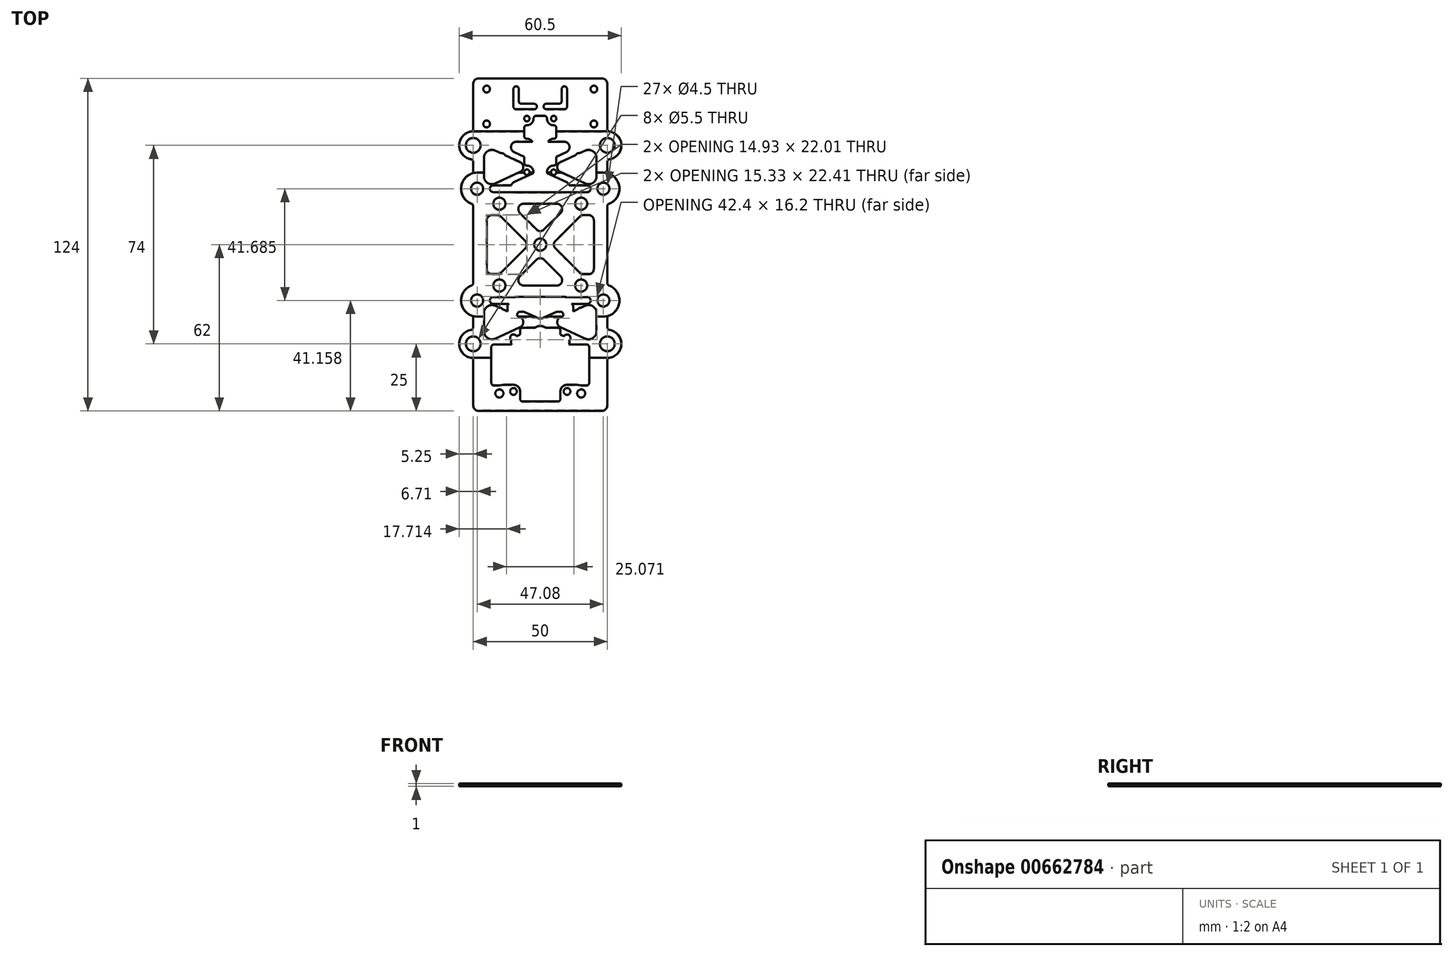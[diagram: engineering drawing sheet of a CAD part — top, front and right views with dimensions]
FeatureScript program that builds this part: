
annotation { "Feature Type Name" : "Feature", "Feature Type Description" : "" }
export const myFeature = defineFeature(function(context is Context, id is Id, definition is map)
    precondition{}
    {
        {
            var Q0;
            Q0=qCreatedBy(makeId("Top.planeOp"),FACE);
            var sketch = newSketch(context, id + "F0", { "sketchPlane" : qUnion([Q0])});
            skLineSegment(sketch, "E0.bottom", {"start": v(15.25, 15.25) * mm, "end": v(-15.25, 15.25) * mm, "construction": true});
            skLineSegment(sketch, "E0.top", {"start": v(15.25, -15.25) * mm, "end": v(-15.25, -15.25) * mm, "construction": true});
            skLineSegment(sketch, "E0.left", {"start": v(15.25, 15.25) * mm, "end": v(15.25, -15.25) * mm, "construction": true});
            skLineSegment(sketch, "E0.right", {"start": v(-15.25, 15.25) * mm, "end": v(-15.25, -15.25) * mm, "construction": true});
            skPoint(sketch, "E0.middle", {"position": v(0, 0) * mm});
            skLineSegment(sketch, "E1", {"start": v(15.25, 15.25) * mm, "end": v(23.54, 20.84) * mm});
            skLineSegment(sketch, "E2", {"start": v(23.54, 20.84) * mm, "end": v(92.7, 67.5) * mm});
            skCircle(sketch, "E3", {"center": v(92.7, 67.5) * mm, "radius": 63.5 * mm, "construction": true});
            skLineSegment(sketch, "E4", {"start": v(0, 0) * mm, "end": v(92.7, 0) * mm, "construction": true});
            skLineSegment(sketch, "E5.bottom", {"start": v(-25, 37) * mm, "end": v(25, 37) * mm, "construction": true});
            skLineSegment(sketch, "E5.top", {"start": v(-25, -37) * mm, "end": v(25, -37) * mm, "construction": true});
            skLineSegment(sketch, "E5.left", {"start": v(-25, 37) * mm, "end": v(-25, -37) * mm, "construction": true});
            skLineSegment(sketch, "E5.right", {"start": v(25, 37) * mm, "end": v(25, -37) * mm, "construction": true});
            skCircle(sketch, "E6", {"center": v(25, 37) * mm, "radius": 4.25 * mm, "construction": true});
            skCircle(sketch, "E7", {"center": v(15.25, 15.25) * mm, "radius": 1.5 * mm, "construction": true});
            skCircle(sketch, "E8", {"center": v(23.54, 20.84) * mm, "radius": 1.5 * mm, "construction": true});
            skCircle(sketch, "E9", {"center": v(92.7, 67.5) * mm, "radius": 50.8 * mm, "construction": true});
            skLineSegment(sketch, "E10.bottom", {"start": v(11.34, 21.05) * mm, "end": v(88.79, 73.3) * mm, "construction": true});
            skLineSegment(sketch, "E10.top", {"start": v(19.16, 9.45) * mm, "end": v(96.62, 61.7) * mm, "construction": true});
            skLineSegment(sketch, "E10.left", {"start": v(11.34, 21.05) * mm, "end": v(19.16, 9.45) * mm, "construction": true});
            skLineSegment(sketch, "E10.right", {"start": v(88.79, 73.3) * mm, "end": v(96.62, 61.7) * mm, "construction": true});
            skCircle(sketch, "E11", {"center": v(-25, 37) * mm, "radius": 4.25 * mm, "construction": true});
            skCircle(sketch, "E12", {"center": v(-25, -37) * mm, "radius": 4.25 * mm, "construction": true});
            skCircle(sketch, "E13", {"center": v(25, -37) * mm, "radius": 4.25 * mm, "construction": true});
            skCircle(sketch, "E14", {"center": v(-15.25, 15.25) * mm, "radius": 1.5 * mm, "construction": true});
            skCircle(sketch, "E15", {"center": v(-15.25, -15.25) * mm, "radius": 1.5 * mm, "construction": true});
            skCircle(sketch, "E16", {"center": v(15.25, -15.25) * mm, "radius": 1.5 * mm, "construction": true});
            skCircle(sketch, "E17.MirrorC", {"center": v(-23.54, 20.84) * mm, "radius": 1.5 * mm, "construction": true});
            skCircle(sketch, "E18.MirrorC", {"center": v(-23.54, -20.84) * mm, "radius": 1.5 * mm, "construction": true});
            skCircle(sketch, "E19.MirrorC", {"center": v(23.54, -20.84) * mm, "radius": 1.5 * mm, "construction": true});
            skSolve(sketch);
        }
        {
            var Q0;
            Q0=qCreatedBy(makeId("Top.planeOp"),FACE);
            var sketch = newSketch(context, id + "F1", { "sketchPlane" : qUnion([Q0])});
            skPoint(sketch, "E20.0", {"position": v(-25, 37) * mm});
            skPoint(sketch, "E21.0", {"position": v(25, 37) * mm});
            skPoint(sketch, "E22.0", {"position": v(25, -37) * mm});
            skPoint(sketch, "E23.0", {"position": v(-25, -37) * mm});
            skCircle(sketch, "E24.0", {"center": v(-23.54, -20.84) * mm, "radius": 1.55 * mm});
            skCircle(sketch, "E25.0", {"center": v(-15.25, -15.25) * mm, "radius": 1.55 * mm});
            skCircle(sketch, "E26.0", {"center": v(15.25, -15.25) * mm, "radius": 1.55 * mm});
            skCircle(sketch, "E27.0", {"center": v(23.54, -20.84) * mm, "radius": 1.55 * mm});
            skCircle(sketch, "E28.0", {"center": v(15.25, 15.25) * mm, "radius": 1.55 * mm});
            skCircle(sketch, "E29.0", {"center": v(-15.25, 15.25) * mm, "radius": 1.55 * mm});
            skCircle(sketch, "E30.0", {"center": v(-23.54, 20.84) * mm, "radius": 1.55 * mm});
            skCircle(sketch, "E31.0", {"center": v(23.54, 20.84) * mm, "radius": 1.55 * mm});
            skCircle(sketch, "E32", {"center": v(25, 37) * mm, "radius": 2.75 * mm});
            skCircle(sketch, "E33", {"center": v(-25, 37) * mm, "radius": 2.75 * mm});
            skCircle(sketch, "E34", {"center": v(-25, -37) * mm, "radius": 2.75 * mm});
            skCircle(sketch, "E35", {"center": v(25, -37) * mm, "radius": 2.75 * mm});
            skSolve(sketch);
        }
        {
            var Q0;
            Q0=qCreatedBy(makeId("Top.planeOp"),FACE);
            var sketch = newSketch(context, id + "F2", { "sketchPlane" : qUnion([Q0])});
            skCircle(sketch, "E36.0", {"center": v(-25, -37) * mm, "radius": 2.75 * mm});
            skCircle(sketch, "E37.0", {"center": v(-23.54, -20.84) * mm, "radius": 1.55 * mm});
            skCircle(sketch, "E38.0", {"center": v(-15.25, -15.25) * mm, "radius": 1.55 * mm});
            skCircle(sketch, "E39.0", {"center": v(15.25, -15.25) * mm, "radius": 1.55 * mm});
            skCircle(sketch, "E40.0", {"center": v(23.54, -20.84) * mm, "radius": 1.55 * mm});
            skCircle(sketch, "E41.0", {"center": v(-25, 37) * mm, "radius": 2.75 * mm});
            skCircle(sketch, "E42.0", {"center": v(-23.54, 20.84) * mm, "radius": 1.55 * mm});
            skCircle(sketch, "E43.0", {"center": v(-15.25, 15.25) * mm, "radius": 1.55 * mm});
            skCircle(sketch, "E44.0", {"center": v(15.25, 15.25) * mm, "radius": 1.55 * mm});
            skCircle(sketch, "E45.0", {"center": v(23.54, 20.84) * mm, "radius": 1.55 * mm});
            skCircle(sketch, "E46.0", {"center": v(25, 37) * mm, "radius": 2.75 * mm});
            skLineSegment(sketch, "E47.bottom", {"start": v(25, 62) * mm, "end": v(-25, 62) * mm});
            skLineSegment(sketch, "E47.top", {"start": v(25, -62) * mm, "end": v(-25, -62) * mm});
            skLineSegment(sketch, "E47.left", {"start": v(25, 62) * mm, "end": v(25, 42.25) * mm});
            skLineSegment(sketch, "E47.right", {"start": v(-25, 62) * mm, "end": v(-25, 42.25) * mm});
            skPoint(sketch, "E47.middle", {"position": v(0, 0) * mm});
            skArc(sketch, "E48", {"start": v(-25, 42.25) * mm, "mid": v(-30.25, 37) * mm, "end": v(-25, 31.75) * mm});
            skArc(sketch, "E49", {"start": v(-25, 26.66) * mm, "mid": v(-29.54, 20.84) * mm, "end": v(-25, 15.02) * mm});
            skArc(sketch, "E50", {"start": v(-25, -15.02) * mm, "mid": v(-29.54, -20.84) * mm, "end": v(-25, -26.66) * mm});
            skArc(sketch, "E51.MirrorCS", {"start": v(25, 42.25) * mm, "mid": v(30.25, 37) * mm, "end": v(25, 31.75) * mm});
            skArc(sketch, "E52.MirrorCS", {"start": v(25, 26.66) * mm, "mid": v(29.54, 20.84) * mm, "end": v(25, 15.02) * mm});
            skArc(sketch, "E53.MirrorCS", {"start": v(25, -15.02) * mm, "mid": v(29.54, -20.84) * mm, "end": v(25, -26.66) * mm});
            skArc(sketch, "E54", {"start": v(-25, -31.75) * mm, "mid": v(-30.25, -37) * mm, "end": v(-25, -42.25) * mm});
            skArc(sketch, "E55.MirrorCS", {"start": v(25, -31.75) * mm, "mid": v(30.25, -37) * mm, "end": v(25, -42.25) * mm});
            skLineSegment(sketch, "E56", {"start": v(-25, 42.25) * mm, "end": v(-25, 39.75) * mm, "construction": true});
            skLineSegment(sketch, "E57", {"start": v(-25, 31.75) * mm, "end": v(-25, 26.66) * mm});
            skLineSegment(sketch, "E58", {"start": v(-25, 34.25) * mm, "end": v(-25, 31.75) * mm, "construction": true});
            skLineSegment(sketch, "E59", {"start": v(-25, 39.75) * mm, "end": v(-25, 34.25) * mm, "construction": true});
            skLineSegment(sketch, "E60", {"start": v(25, 39.75) * mm, "end": v(25, 34.25) * mm, "construction": true});
            skLineSegment(sketch, "E61", {"start": v(25, 42.25) * mm, "end": v(25, 39.75) * mm, "construction": true});
            skLineSegment(sketch, "E62", {"start": v(25, 34.25) * mm, "end": v(25, 31.75) * mm, "construction": true});
            skLineSegment(sketch, "E63", {"start": v(25, 31.75) * mm, "end": v(25, 26.66) * mm});
            skLineSegment(sketch, "E64", {"start": v(-25, 26.66) * mm, "end": v(-25, 15.02) * mm, "construction": true});
            skLineSegment(sketch, "E65", {"start": v(-25, 15.02) * mm, "end": v(-25, -15.02) * mm});
            skLineSegment(sketch, "E66", {"start": v(25, 26.66) * mm, "end": v(25, 15.02) * mm, "construction": true});
            skLineSegment(sketch, "E67", {"start": v(25, 15.02) * mm, "end": v(25, -15.02) * mm});
            skLineSegment(sketch, "E68", {"start": v(-25, -31.75) * mm, "end": v(-25, -34.25) * mm, "construction": true});
            skLineSegment(sketch, "E69", {"start": v(-25, -42.25) * mm, "end": v(-25, -62) * mm});
            skLineSegment(sketch, "E70", {"start": v(-25, -39.75) * mm, "end": v(-25, -42.25) * mm, "construction": true});
            skLineSegment(sketch, "E71", {"start": v(-25, -34.25) * mm, "end": v(-25, -39.75) * mm, "construction": true});
            skLineSegment(sketch, "E72", {"start": v(-25, -26.66) * mm, "end": v(-25, -31.75) * mm});
            skLineSegment(sketch, "E73", {"start": v(-25, -15.02) * mm, "end": v(-25, -26.66) * mm, "construction": true});
            skLineSegment(sketch, "E74", {"start": v(25, -15.02) * mm, "end": v(25, -26.66) * mm});
            skLineSegment(sketch, "E75", {"start": v(25, -26.66) * mm, "end": v(25, -31.75) * mm});
            skLineSegment(sketch, "E76", {"start": v(25, -31.75) * mm, "end": v(25, -42.25) * mm, "construction": true});
            skLineSegment(sketch, "E77", {"start": v(25, -42.25) * mm, "end": v(25, -42.25) * mm});
            skArc(sketch, "E78", {"start": v(25, -34.25) * mm, "mid": v(22.25, -37) * mm, "end": v(25, -39.75) * mm});
            skArc(sketch, "E79", {"start": v(25, -39.75) * mm, "mid": v(27.75, -37) * mm, "end": v(25, -34.25) * mm});
            skLineSegment(sketch, "E80", {"start": v(25, -42.25) * mm, "end": v(25, -62) * mm});
            skSolve(sketch);
        }
        {
            var Q0;
            Q0 = qSketchRegion(id + "F2", true);
            extrude(context, id + "F3", {"entities" : qUnion([Q0]), "depth" : 1 * mm, "offsetDistance" : 25 * mm});
        }
        {
            var Q0;
            Q0=qCreatedBy(makeId("Top.planeOp"),FACE);
            var sketch = newSketch(context, id + "F4", { "sketchPlane" : qUnion([Q0])});
            skCircle(sketch, "E81.0", {"center": v(-23.54, 20.84) * mm, "radius": 1.55 * mm});
            skCircle(sketch, "E82.0", {"center": v(-15.25, 15.25) * mm, "radius": 1.55 * mm});
            skCircle(sketch, "E83.0", {"center": v(15.25, 15.25) * mm, "radius": 1.55 * mm});
            skCircle(sketch, "E84.0", {"center": v(23.54, 20.84) * mm, "radius": 1.55 * mm});
            skCircle(sketch, "E85.0", {"center": v(-15.25, -15.25) * mm, "radius": 1.55 * mm});
            skCircle(sketch, "E86.0", {"center": v(-23.54, -20.84) * mm, "radius": 1.55 * mm});
            skCircle(sketch, "E87.0", {"center": v(15.25, -15.25) * mm, "radius": 1.55 * mm});
            skCircle(sketch, "E88.0", {"center": v(23.54, -20.84) * mm, "radius": 1.55 * mm});
            skArc(sketch, "E89.0", {"start": v(-25, 26.66) * mm, "mid": v(-29.54, 20.84) * mm, "end": v(-25, 15.02) * mm});
            skLineSegment(sketch, "E90.0", {"start": v(-25, 15.02) * mm, "end": v(-25, -15.02) * mm});
            skArc(sketch, "E91.0", {"start": v(-25, -15.02) * mm, "mid": v(-29.54, -20.84) * mm, "end": v(-25, -26.66) * mm});
            skLineSegment(sketch, "E92.0", {"start": v(25, 15.02) * mm, "end": v(25, -15.02) * mm});
            skArc(sketch, "E93.0", {"start": v(25, 26.66) * mm, "mid": v(29.54, 20.84) * mm, "end": v(25, 15.02) * mm});
            skArc(sketch, "E94.0", {"start": v(25, -15.02) * mm, "mid": v(29.54, -20.84) * mm, "end": v(25, -26.66) * mm});
            skArc(sketch, "E95", {"start": v(-25, 26.66) * mm, "mid": v(-24.28, 26.8) * mm, "end": v(-23.54, 26.84) * mm});
            skArc(sketch, "E96", {"start": v(-25, -26.66) * mm, "mid": v(-24.28, -26.8) * mm, "end": v(-23.54, -26.84) * mm});
            skArc(sketch, "E97", {"start": v(25, 26.66) * mm, "mid": v(24.28, 26.8) * mm, "end": v(23.54, 26.84) * mm});
            skArc(sketch, "E98", {"start": v(25, -26.66) * mm, "mid": v(24.28, -26.8) * mm, "end": v(23.54, -26.84) * mm});
            skLineSegment(sketch, "E99", {"start": v(-23.54, 26.84) * mm, "end": v(23.54, 26.84) * mm});
            skLineSegment(sketch, "E100", {"start": v(-23.54, -26.84) * mm, "end": v(23.54, -26.84) * mm});
            skSolve(sketch);
        }
        {
            var Q0;
            Q0=qCreatedBy(makeId("Top.planeOp"),FACE);
            var sketch = newSketch(context, id + "F5", { "sketchPlane" : qUnion([Q0])});
            skArc(sketch, "E101.0.0", {"start": v(25, -26.66) * mm, "mid": v(29.54, -20.84) * mm, "end": v(25, -15.02) * mm});
            skLineSegment(sketch, "E101.0.1", {"start": v(25, -15.02) * mm, "end": v(25, 15.02) * mm});
            skArc(sketch, "E101.0.2", {"start": v(25, 15.02) * mm, "mid": v(29.54, 20.84) * mm, "end": v(25, 26.66) * mm});
            skLineSegment(sketch, "E101.0.3", {"start": v(25, 26.66) * mm, "end": v(25, 31.75) * mm});
            skArc(sketch, "E101.0.4", {"start": v(25, 31.75) * mm, "mid": v(30.25, 37) * mm, "end": v(25, 42.25) * mm});
            skLineSegment(sketch, "E101.0.5", {"start": v(25, 42.25) * mm, "end": v(25, 62) * mm});
            skLineSegment(sketch, "E101.0.6", {"start": v(25, 62) * mm, "end": v(-25, 62) * mm, "construction": true});
            skLineSegment(sketch, "E101.0.7", {"start": v(-25, 62) * mm, "end": v(-25, 42.25) * mm});
            skArc(sketch, "E101.0.8", {"start": v(-25, 42.25) * mm, "mid": v(-30.25, 37) * mm, "end": v(-25, 31.75) * mm});
            skLineSegment(sketch, "E101.0.9", {"start": v(-25, 31.75) * mm, "end": v(-25, 26.66) * mm});
            skArc(sketch, "E101.0.10", {"start": v(-25, 26.66) * mm, "mid": v(-29.54, 20.84) * mm, "end": v(-25, 15.02) * mm});
            skLineSegment(sketch, "E101.0.11", {"start": v(-25, 15.02) * mm, "end": v(-25, -15.02) * mm});
            skArc(sketch, "E101.0.12", {"start": v(-25, -15.02) * mm, "mid": v(-29.54, -20.84) * mm, "end": v(-25, -26.66) * mm});
            skLineSegment(sketch, "E101.0.13", {"start": v(-25, -26.66) * mm, "end": v(-25, -31.75) * mm});
            skArc(sketch, "E101.0.14", {"start": v(-25, -31.75) * mm, "mid": v(-30.25, -37) * mm, "end": v(-25, -42.25) * mm});
            skLineSegment(sketch, "E101.0.15", {"start": v(-25, -42.25) * mm, "end": v(-25, -62) * mm});
            skLineSegment(sketch, "E101.0.16", {"start": v(-25, -62) * mm, "end": v(25, -62) * mm, "construction": true});
            skLineSegment(sketch, "E101.0.17", {"start": v(25, -62) * mm, "end": v(25, -42.25) * mm});
            skArc(sketch, "E101.0.18", {"start": v(25, -42.25) * mm, "mid": v(30.25, -37) * mm, "end": v(25, -31.75) * mm});
            skLineSegment(sketch, "E101.0.19", {"start": v(25, -31.75) * mm, "end": v(25, -26.66) * mm});
            skLineSegment(sketch, "E102", {"start": v(-25, 42.25) * mm, "end": v(25, 42.25) * mm});
            skLineSegment(sketch, "E103", {"start": v(-25, -42.25) * mm, "end": v(25, -42.25) * mm});
            skCircle(sketch, "E104.0", {"center": v(-25, 37) * mm, "radius": 2.75 * mm});
            skCircle(sketch, "E105.0", {"center": v(-23.54, 20.84) * mm, "radius": 1.55 * mm});
            skCircle(sketch, "E106.0", {"center": v(-15.25, 15.25) * mm, "radius": 1.55 * mm});
            skCircle(sketch, "E107.0", {"center": v(15.25, 15.25) * mm, "radius": 1.55 * mm});
            skCircle(sketch, "E108.0", {"center": v(23.54, 20.84) * mm, "radius": 1.55 * mm});
            skCircle(sketch, "E109.0", {"center": v(25, 37) * mm, "radius": 2.75 * mm});
            skCircle(sketch, "E110.0", {"center": v(-23.54, -20.84) * mm, "radius": 1.55 * mm});
            skCircle(sketch, "E111.0", {"center": v(-15.25, -15.25) * mm, "radius": 1.55 * mm});
            skCircle(sketch, "E112.0", {"center": v(15.25, -15.25) * mm, "radius": 1.55 * mm});
            skCircle(sketch, "E113.0", {"center": v(23.54, -20.84) * mm, "radius": 1.55 * mm});
            skCircle(sketch, "E114.0", {"center": v(-25, -37) * mm, "radius": 2.75 * mm});
            skCircle(sketch, "E115.0", {"center": v(25, -37) * mm, "radius": 2.75 * mm});
            skSolve(sketch);
        }
        {
            var Q0;
            Q0 = qSketchRegion(id + "F4", true);
            extrude(context, id + "F6", {"entities" : qUnion([Q0]), "depth" : 1 * mm, "offsetDistance" : 25 * mm});
        }
        {
            var Q0;
            Q0 = qSketchRegion(id + "F5", true);
            extrude(context, id + "F7", {"entities" : qUnion([Q0]), "depth" : 1 * mm, "offsetDistance" : 25 * mm});
        }
        {
            var Q0;
            Q0=makeQuery(id+"F3.opExtrude","SWEPT_EDGE",EDGE,{"disambiguationData":[OSD([sQuery(id+"F2.wireOp",EDGE,"E47.top"),sQuery(id+"F2.wireOp",EDGE,"E69")])]});
            var Q1;
            Q1=makeQuery(id+"F3.opExtrude","SWEPT_EDGE",EDGE,{"disambiguationData":[OSD([sQuery(id+"F2.wireOp",EDGE,"E47.top"),sQuery(id+"F2.wireOp",EDGE,"E80")])]});
            var Q2;
            Q2=makeQuery(id+"F3.opExtrude","SWEPT_EDGE",EDGE,{"disambiguationData":[OSD([sQuery(id+"F2.wireOp",EDGE,"E47.bottom"),sQuery(id+"F2.wireOp",EDGE,"E47.right")])]});
            var Q3;
            Q3=makeQuery(id+"F3.opExtrude","SWEPT_EDGE",EDGE,{"disambiguationData":[OSD([sQuery(id+"F2.wireOp",EDGE,"E47.bottom"),sQuery(id+"F2.wireOp",EDGE,"E47.left")])]});
            fillet(context, id + "F8", {"entities" : qUnion([Q0, Q1, Q2, Q3]), "radius" : 2 * mm, "allowEdgeOverflow" : false});
        }
        {
            var Q0;
            Q0=makeQuery(id+"F3.opExtrude","SWEPT_EDGE",EDGE,{"disambiguationData":[OSD([sQuery(id+"F2.wireOp",EDGE,"E47.left"),sQuery(id+"F2.wireOp",EDGE,"E51.MirrorCS")])]});
            var Q1;
            Q1=makeQuery(id+"F3.opExtrude","SWEPT_EDGE",EDGE,{"disambiguationData":[OSD([sQuery(id+"F2.wireOp",EDGE,"E51.MirrorCS"),sQuery(id+"F2.wireOp",EDGE,"E63")])]});
            var Q2;
            Q2=makeQuery(id+"F3.opExtrude","SWEPT_EDGE",EDGE,{"disambiguationData":[OSD([sQuery(id+"F2.wireOp",EDGE,"E52.MirrorCS"),sQuery(id+"F2.wireOp",EDGE,"E63")])]});
            var Q3;
            Q3=makeQuery(id+"F3.opExtrude","SWEPT_EDGE",EDGE,{"disambiguationData":[OSD([sQuery(id+"F2.wireOp",EDGE,"E52.MirrorCS"),sQuery(id+"F2.wireOp",EDGE,"E67")])]});
            var Q4;
            Q4=makeQuery(id+"F3.opExtrude","SWEPT_EDGE",EDGE,{"disambiguationData":[OSD([sQuery(id+"F2.wireOp",EDGE,"E53.MirrorCS"),sQuery(id+"F2.wireOp",EDGE,"E67"),sQuery(id+"F2.wireOp",EDGE,"E74")])]});
            var Q5;
            Q5=makeQuery(id+"F3.opExtrude","SWEPT_EDGE",EDGE,{"disambiguationData":[OSD([sQuery(id+"F2.wireOp",EDGE,"E55.MirrorCS"),sQuery(id+"F2.wireOp",EDGE,"E75")])]});
            var Q6;
            Q6=makeQuery(id+"F3.opExtrude","SWEPT_EDGE",EDGE,{"disambiguationData":[OSD([sQuery(id+"F2.wireOp",EDGE,"E55.MirrorCS"),sQuery(id+"F2.wireOp",EDGE,"E80")])]});
            var Q7;
            Q7=makeQuery(id+"F3.opExtrude","SWEPT_EDGE",EDGE,{"disambiguationData":[OSD([sQuery(id+"F2.wireOp",EDGE,"E47.right"),sQuery(id+"F2.wireOp",EDGE,"E48")])]});
            var Q8;
            Q8=makeQuery(id+"F3.opExtrude","SWEPT_EDGE",EDGE,{"disambiguationData":[OSD([sQuery(id+"F2.wireOp",EDGE,"E49"),sQuery(id+"F2.wireOp",EDGE,"E57")])]});
            var Q9;
            Q9=makeQuery(id+"F3.opExtrude","SWEPT_EDGE",EDGE,{"disambiguationData":[OSD([sQuery(id+"F2.wireOp",EDGE,"E48"),sQuery(id+"F2.wireOp",EDGE,"E57")])]});
            var Q10;
            Q10=makeQuery(id+"F3.opExtrude","SWEPT_EDGE",EDGE,{"disambiguationData":[OSD([sQuery(id+"F2.wireOp",EDGE,"E49"),sQuery(id+"F2.wireOp",EDGE,"E65")])]});
            var Q11;
            Q11=makeQuery(id+"F3.opExtrude","SWEPT_EDGE",EDGE,{"disambiguationData":[OSD([sQuery(id+"F2.wireOp",EDGE,"E50"),sQuery(id+"F2.wireOp",EDGE,"E72")])]});
            var Q12;
            Q12=makeQuery(id+"F3.opExtrude","SWEPT_EDGE",EDGE,{"disambiguationData":[OSD([sQuery(id+"F2.wireOp",EDGE,"E50"),sQuery(id+"F2.wireOp",EDGE,"E65")])]});
            var Q13;
            Q13=makeQuery(id+"F3.opExtrude","SWEPT_EDGE",EDGE,{"disambiguationData":[OSD([sQuery(id+"F2.wireOp",EDGE,"E54"),sQuery(id+"F2.wireOp",EDGE,"E72")])]});
            var Q14;
            Q14=makeQuery(id+"F3.opExtrude","SWEPT_EDGE",EDGE,{"disambiguationData":[OSD([sQuery(id+"F2.wireOp",EDGE,"E54"),sQuery(id+"F2.wireOp",EDGE,"E69")])]});
            var Q15;
            Q15=makeQuery(id+"F7.opExtrude","SWEPT_EDGE",EDGE,{"disambiguationData":[OSD([sQuery(id+"F5.wireOp",EDGE,"E101.0.9"),sQuery(id+"F5.wireOp",EDGE,"E101.0.10")])]});
            var Q16;
            Q16=makeQuery(id+"F7.opExtrude","SWEPT_EDGE",EDGE,{"disambiguationData":[OSD([sQuery(id+"F5.wireOp",EDGE,"E101.0.8"),sQuery(id+"F5.wireOp",EDGE,"E101.0.9")])]});
            var Q17;
            Q17=makeQuery(id+"F7.opExtrude","SWEPT_EDGE",EDGE,{"disambiguationData":[OSD([sQuery(id+"F5.wireOp",EDGE,"E101.0.10"),sQuery(id+"F5.wireOp",EDGE,"E101.0.11")])]});
            var Q18;
            Q18=makeQuery(id+"F7.opExtrude","SWEPT_EDGE",EDGE,{"disambiguationData":[OSD([sQuery(id+"F5.wireOp",EDGE,"E101.0.11"),sQuery(id+"F5.wireOp",EDGE,"E101.0.12")])]});
            var Q19;
            Q19=makeQuery(id+"F7.opExtrude","SWEPT_EDGE",EDGE,{"disambiguationData":[OSD([sQuery(id+"F5.wireOp",EDGE,"E101.0.12"),sQuery(id+"F5.wireOp",EDGE,"E101.0.13")])]});
            var Q20;
            Q20=makeQuery(id+"F7.opExtrude","SWEPT_EDGE",EDGE,{"disambiguationData":[OSD([sQuery(id+"F5.wireOp",EDGE,"E101.0.13"),sQuery(id+"F5.wireOp",EDGE,"E101.0.14")])]});
            var Q21;
            Q21=makeQuery(id+"F7.opExtrude","SWEPT_EDGE",EDGE,{"disambiguationData":[OSD([sQuery(id+"F5.wireOp",EDGE,"E101.0.1"),sQuery(id+"F5.wireOp",EDGE,"E101.0.2")])]});
            var Q22;
            Q22=makeQuery(id+"F7.opExtrude","SWEPT_EDGE",EDGE,{"disambiguationData":[OSD([sQuery(id+"F5.wireOp",EDGE,"E101.0.2"),sQuery(id+"F5.wireOp",EDGE,"E101.0.3")])]});
            var Q23;
            Q23=makeQuery(id+"F7.opExtrude","SWEPT_EDGE",EDGE,{"disambiguationData":[OSD([sQuery(id+"F5.wireOp",EDGE,"E101.0.3"),sQuery(id+"F5.wireOp",EDGE,"E101.0.4")])]});
            var Q24;
            Q24=makeQuery(id+"F7.opExtrude","SWEPT_EDGE",EDGE,{"disambiguationData":[OSD([sQuery(id+"F5.wireOp",EDGE,"E101.0.18"),sQuery(id+"F5.wireOp",EDGE,"E101.0.19")])]});
            var Q25;
            Q25=makeQuery(id+"F7.opExtrude","SWEPT_EDGE",EDGE,{"disambiguationData":[OSD([sQuery(id+"F5.wireOp",EDGE,"E101.0.0"),sQuery(id+"F5.wireOp",EDGE,"E101.0.19")])]});
            var Q26;
            Q26=makeQuery(id+"F7.opExtrude","SWEPT_EDGE",EDGE,{"disambiguationData":[OSD([sQuery(id+"F5.wireOp",EDGE,"E101.0.0"),sQuery(id+"F5.wireOp",EDGE,"E101.0.1")])]});
            var Q27;
            Q27=makeQuery(id+"F3.opExtrude","SWEPT_EDGE",EDGE,{"disambiguationData":[OSD([sQuery(id+"F2.wireOp",EDGE,"E53.MirrorCS"),sQuery(id+"F2.wireOp",EDGE,"E74"),sQuery(id+"F2.wireOp",EDGE,"E75")])]});
            var Q28;
            Q28=makeQuery(id+"F6.opExtrude","SWEPT_EDGE",EDGE,{"disambiguationData":[OSD([sQuery(id+"F4.wireOp",EDGE,"E92.0"),sQuery(id+"F4.wireOp",EDGE,"E94.0")])]});
            var Q29;
            Q29=makeQuery(id+"F6.opExtrude","SWEPT_EDGE",EDGE,{"disambiguationData":[OSD([sQuery(id+"F4.wireOp",EDGE,"E92.0"),sQuery(id+"F4.wireOp",EDGE,"E93.0")])]});
            var Q30;
            Q30=makeQuery(id+"F6.opExtrude","SWEPT_EDGE",EDGE,{"disambiguationData":[OSD([sQuery(id+"F4.wireOp",EDGE,"E89.0"),sQuery(id+"F4.wireOp",EDGE,"E90.0")])]});
            var Q31;
            Q31=makeQuery(id+"F6.opExtrude","SWEPT_EDGE",EDGE,{"disambiguationData":[OSD([sQuery(id+"F4.wireOp",EDGE,"E90.0"),sQuery(id+"F4.wireOp",EDGE,"E91.0")])]});
            fillet(context, id + "F9", {"entities" : qUnion([Q0, Q1, Q2, Q3, Q4, Q5, Q6, Q7, Q8, Q9, Q10, Q11, Q12, Q13, Q14, Q15, Q16, Q17, Q18, Q19, Q20, Q21, Q22, Q23, Q24, Q25, Q26, Q27, Q28, Q29, Q30, Q31]), "radius" : 1 * mm, "allowEdgeOverflow" : false});
        }
        {
            var Q0;
            Q0=makeQuery(id+"F3.opExtrude","CAP_FACE",FACE,{"disambiguationData":[OSD([sQuery(id+"F2.wireOp",EDGE,"E36.0"),sQuery(id+"F2.wireOp",EDGE,"E37.0"),sQuery(id+"F2.wireOp",EDGE,"E38.0"),sQuery(id+"F2.wireOp",EDGE,"E39.0"),sQuery(id+"F2.wireOp",EDGE,"E40.0"),sQuery(id+"F2.wireOp",EDGE,"E41.0"),sQuery(id+"F2.wireOp",EDGE,"E42.0"),sQuery(id+"F2.wireOp",EDGE,"E43.0"),sQuery(id+"F2.wireOp",EDGE,"E44.0"),sQuery(id+"F2.wireOp",EDGE,"E45.0"),sQuery(id+"F2.wireOp",EDGE,"E46.0"),sQuery(id+"F2.wireOp",EDGE,"E47.bottom"),sQuery(id+"F2.wireOp",EDGE,"E47.top"),sQuery(id+"F2.wireOp",EDGE,"E47.left"),sQuery(id+"F2.wireOp",EDGE,"E47.right"),sQuery(id+"F2.wireOp",EDGE,"E48"),sQuery(id+"F2.wireOp",EDGE,"E49"),sQuery(id+"F2.wireOp",EDGE,"E50"),sQuery(id+"F2.wireOp",EDGE,"E51.MirrorCS"),sQuery(id+"F2.wireOp",EDGE,"E52.MirrorCS"),sQuery(id+"F2.wireOp",EDGE,"E53.MirrorCS"),sQuery(id+"F2.wireOp",EDGE,"E54"),sQuery(id+"F2.wireOp",EDGE,"E55.MirrorCS"),sQuery(id+"F2.wireOp",EDGE,"rjWOpLop-ofpK-hTEo-auwK-LkPdoEbubAMj"),sQuery(id+"F2.wireOp",EDGE,"E57"),sQuery(id+"F2.wireOp",EDGE,"E63"),sQuery(id+"F2.wireOp",EDGE,"E65"),sQuery(id+"F2.wireOp",EDGE,"E67"),sQuery(id+"F2.wireOp",EDGE,"E69"),sQuery(id+"F2.wireOp",EDGE,"E72"),sQuery(id+"F2.wireOp",EDGE,"E75"),sQuery(id+"F2.wireOp",EDGE,"E78"),sQuery(id+"F2.wireOp",EDGE,"E79"),sQuery(id+"F2.wireOp",EDGE,"E80")])],"isStart":false});
            var sketch = newSketch(context, id + "F10", { "sketchPlane" : qUnion([Q0])});
            skLineSegment(sketch, "E116.0.0", {"start": v(25, 43.17) * mm, "end": v(25, 60) * mm, "construction": true});
            skArc(sketch, "E116.0.1", {"start": v(25, 60) * mm, "mid": v(24.41, 61.41) * mm, "end": v(23, 62) * mm, "construction": true});
            skLineSegment(sketch, "E116.0.2", {"start": v(23, 62) * mm, "end": v(-23, 62) * mm, "construction": true});
            skArc(sketch, "E116.0.3", {"start": v(-23, 62) * mm, "mid": v(-24.41, 61.41) * mm, "end": v(-25, 60) * mm, "construction": true});
            skLineSegment(sketch, "E116.0.4", {"start": v(-25, 60) * mm, "end": v(-25, 43.17) * mm, "construction": true});
            skArc(sketch, "E116.0.5", {"start": v(-25, 43.17) * mm, "mid": v(-25.24, 42.52) * mm, "end": v(-25.84, 42.18) * mm, "construction": true});
            skArc(sketch, "E116.0.6", {"start": v(-25.84, 42.18) * mm, "mid": v(-30.25, 37) * mm, "end": v(-25.84, 31.82) * mm, "construction": true});
            skArc(sketch, "E116.0.7", {"start": v(-25.84, 31.82) * mm, "mid": v(-25.24, 31.48) * mm, "end": v(-25, 30.83) * mm, "construction": true});
            skLineSegment(sketch, "E116.0.8", {"start": v(-25, 30.83) * mm, "end": v(-25, 27.4) * mm, "construction": true});
            skArc(sketch, "E116.0.9", {"start": v(-25, 27.4) * mm, "mid": v(-25.18, 26.83) * mm, "end": v(-25.65, 26.46) * mm, "construction": true});
            skArc(sketch, "E116.0.10", {"start": v(-25.65, 26.46) * mm, "mid": v(-29.54, 20.84) * mm, "end": v(-25.65, 15.23) * mm, "construction": true});
            skArc(sketch, "E116.0.11", {"start": v(-25.65, 15.23) * mm, "mid": v(-25.18, 14.86) * mm, "end": v(-25, 14.29) * mm, "construction": true});
            skLineSegment(sketch, "E116.0.12", {"start": v(-25, 14.29) * mm, "end": v(-25, -14.29) * mm, "construction": true});
            skArc(sketch, "E116.0.13", {"start": v(-25, -14.29) * mm, "mid": v(-25.18, -14.86) * mm, "end": v(-25.65, -15.23) * mm, "construction": true});
            skArc(sketch, "E116.0.14", {"start": v(-25.65, -15.23) * mm, "mid": v(-29.54, -20.84) * mm, "end": v(-25.65, -26.46) * mm, "construction": true});
            skArc(sketch, "E116.0.15", {"start": v(-25.65, -26.46) * mm, "mid": v(-25.18, -26.83) * mm, "end": v(-25, -27.4) * mm, "construction": true});
            skLineSegment(sketch, "E116.0.16", {"start": v(-25, -27.4) * mm, "end": v(-25, -30.83) * mm, "construction": true});
            skArc(sketch, "E116.0.17", {"start": v(-25, -30.83) * mm, "mid": v(-25.24, -31.48) * mm, "end": v(-25.84, -31.82) * mm, "construction": true});
            skArc(sketch, "E116.0.18", {"start": v(-25.84, -31.82) * mm, "mid": v(-30.25, -37) * mm, "end": v(-25.84, -42.18) * mm, "construction": true});
            skArc(sketch, "E116.0.19", {"start": v(-25.84, -42.18) * mm, "mid": v(-25.24, -42.52) * mm, "end": v(-25, -43.17) * mm, "construction": true});
            skLineSegment(sketch, "E116.0.20", {"start": v(-25, -43.17) * mm, "end": v(-25, -60) * mm, "construction": true});
            skArc(sketch, "E116.0.21", {"start": v(-25, -60) * mm, "mid": v(-24.41, -61.41) * mm, "end": v(-23, -62) * mm, "construction": true});
            skLineSegment(sketch, "E116.0.22", {"start": v(-23, -62) * mm, "end": v(23, -62) * mm, "construction": true});
            skArc(sketch, "E116.0.23", {"start": v(23, -62) * mm, "mid": v(24.41, -61.41) * mm, "end": v(25, -60) * mm, "construction": true});
            skLineSegment(sketch, "E116.0.24", {"start": v(25, -60) * mm, "end": v(25, -43.17) * mm, "construction": true});
            skArc(sketch, "E116.0.25", {"start": v(25, -43.17) * mm, "mid": v(25.24, -42.52) * mm, "end": v(25.84, -42.18) * mm, "construction": true});
            skArc(sketch, "E116.0.26", {"start": v(25.84, -42.18) * mm, "mid": v(30.25, -37) * mm, "end": v(25.84, -31.82) * mm, "construction": true});
            skArc(sketch, "E116.0.27", {"start": v(25.84, -31.82) * mm, "mid": v(25.24, -31.48) * mm, "end": v(25, -30.83) * mm, "construction": true});
            skLineSegment(sketch, "E116.0.28", {"start": v(25, -30.83) * mm, "end": v(25, -27.4) * mm, "construction": true});
            skArc(sketch, "E116.0.29", {"start": v(25, -27.4) * mm, "mid": v(25.18, -26.83) * mm, "end": v(25.65, -26.46) * mm, "construction": true});
            skArc(sketch, "E116.0.30", {"start": v(25.65, -26.46) * mm, "mid": v(29.54, -20.84) * mm, "end": v(25.65, -15.23) * mm, "construction": true});
            skArc(sketch, "E116.0.31", {"start": v(25.65, -15.23) * mm, "mid": v(25.18, -14.86) * mm, "end": v(25, -14.29) * mm, "construction": true});
            skLineSegment(sketch, "E116.0.32", {"start": v(25, -14.29) * mm, "end": v(25, 14.29) * mm, "construction": true});
            skArc(sketch, "E116.0.33", {"start": v(25, 14.29) * mm, "mid": v(25.18, 14.86) * mm, "end": v(25.65, 15.23) * mm, "construction": true});
            skArc(sketch, "E116.0.34", {"start": v(25.65, 15.23) * mm, "mid": v(29.54, 20.84) * mm, "end": v(25.65, 26.46) * mm, "construction": true});
            skArc(sketch, "E116.0.35", {"start": v(25.65, 26.46) * mm, "mid": v(25.18, 26.83) * mm, "end": v(25, 27.4) * mm, "construction": true});
            skLineSegment(sketch, "E116.0.36", {"start": v(25, 27.4) * mm, "end": v(25, 30.83) * mm, "construction": true});
            skArc(sketch, "E116.0.37", {"start": v(25, 30.83) * mm, "mid": v(25.24, 31.48) * mm, "end": v(25.84, 31.82) * mm, "construction": true});
            skArc(sketch, "E116.0.38", {"start": v(25.84, 31.82) * mm, "mid": v(30.25, 37) * mm, "end": v(25.84, 42.18) * mm, "construction": true});
            skArc(sketch, "E116.0.39", {"start": v(25.84, 42.18) * mm, "mid": v(25.24, 42.52) * mm, "end": v(25, 43.17) * mm, "construction": true});
            skCircle(sketch, "E117", {"center": v(-23.54, -20.84) * mm, "radius": 2.25 * mm});
            skCircle(sketch, "E118", {"center": v(-15.25, -15.25) * mm, "radius": 2.25 * mm});
            skCircle(sketch, "E119", {"center": v(15.25, -15.25) * mm, "radius": 2.25 * mm});
            skCircle(sketch, "E120", {"center": v(23.54, -20.84) * mm, "radius": 2.25 * mm});
            skCircle(sketch, "E121", {"center": v(-15.25, 15.25) * mm, "radius": 2.25 * mm});
            skCircle(sketch, "E122", {"center": v(-23.54, 20.84) * mm, "radius": 2.25 * mm});
            skCircle(sketch, "E123", {"center": v(15.25, 15.25) * mm, "radius": 2.25 * mm});
            skCircle(sketch, "E124", {"center": v(23.54, 20.84) * mm, "radius": 2.25 * mm});
            skLineSegment(sketch, "E125.bottom", {"start": v(10, -34.75) * mm, "end": v(-10, -34.75) * mm, "construction": true});
            skLineSegment(sketch, "E125.top", {"start": v(10, -54.75) * mm, "end": v(-10, -54.75) * mm, "construction": true});
            skLineSegment(sketch, "E125.left", {"start": v(10, -34.75) * mm, "end": v(10, -54.75) * mm, "construction": true});
            skLineSegment(sketch, "E125.right", {"start": v(-10, -34.75) * mm, "end": v(-10, -54.75) * mm, "construction": true});
            skPoint(sketch, "E125.middle", {"position": v(0, -44.75) * mm});
            skCircle(sketch, "E126", {"center": v(-10, -34.75) * mm, "radius": 1.25 * mm});
            skCircle(sketch, "E127", {"center": v(10, -34.75) * mm, "radius": 1.25 * mm});
            skCircle(sketch, "E128", {"center": v(10, -54.75) * mm, "radius": 1.25 * mm});
            skCircle(sketch, "E129", {"center": v(-10, -54.75) * mm, "radius": 1.25 * mm});
            skLineSegment(sketch, "E130.bottom", {"start": v(15.25, -25) * mm, "end": v(-15.25, -25) * mm, "construction": true});
            skLineSegment(sketch, "E130.top", {"start": v(15.25, -55.5) * mm, "end": v(-15.25, -55.5) * mm, "construction": true});
            skLineSegment(sketch, "E130.left", {"start": v(15.25, -25) * mm, "end": v(15.25, -55.5) * mm, "construction": true});
            skLineSegment(sketch, "E130.right", {"start": v(-15.25, -25) * mm, "end": v(-15.25, -55.5) * mm, "construction": true});
            skPoint(sketch, "E130.middle", {"position": v(0, -40.25) * mm});
            skCircle(sketch, "E131", {"center": v(15.25, -25) * mm, "radius": 1.5 * mm});
            skCircle(sketch, "E132", {"center": v(-15.25, -25) * mm, "radius": 1.5 * mm});
            skCircle(sketch, "E133", {"center": v(-15.25, -55.5) * mm, "radius": 1.5 * mm});
            skCircle(sketch, "E134", {"center": v(15.25, -55.5) * mm, "radius": 1.5 * mm});
            skLineSegment(sketch, "E135.bottom", {"start": v(18, -22.25) * mm, "end": v(-18, -22.25) * mm, "construction": true});
            skLineSegment(sketch, "E135.top", {"start": v(18, -58.25) * mm, "end": v(-18, -58.25) * mm, "construction": true});
            skLineSegment(sketch, "E135.left", {"start": v(18, -22.25) * mm, "end": v(18, -58.25) * mm, "construction": true});
            skLineSegment(sketch, "E135.right", {"start": v(-18, -22.25) * mm, "end": v(-18, -58.25) * mm, "construction": true});
            skLineSegment(sketch, "E136.bottom", {"start": v(13.5, -31.25) * mm, "end": v(-13.5, -31.25) * mm, "construction": true});
            skLineSegment(sketch, "E136.top", {"start": v(13.5, -58.25) * mm, "end": v(-13.5, -58.25) * mm, "construction": true});
            skLineSegment(sketch, "E136.left", {"start": v(13.5, -31.25) * mm, "end": v(13.5, -58.25) * mm, "construction": true});
            skLineSegment(sketch, "E136.right", {"start": v(-13.5, -31.25) * mm, "end": v(-13.5, -55.5) * mm, "construction": true});
            skArc(sketch, "E137", {"start": v(-10, -52.25) * mm, "mid": v(-8.23, -52.98) * mm, "end": v(-7.5, -54.75) * mm});
            skArc(sketch, "E138", {"start": v(-10, -37.25) * mm, "mid": v(-8.23, -36.52) * mm, "end": v(-7.5, -34.75) * mm});
            skArc(sketch, "E139", {"start": v(7.5, -34.75) * mm, "mid": v(8.23, -36.52) * mm, "end": v(10, -37.25) * mm});
            skArc(sketch, "E140", {"start": v(10, -52.25) * mm, "mid": v(8.23, -52.98) * mm, "end": v(7.5, -54.75) * mm});
            skLineSegment(sketch, "E141.0", {"start": v(18.25, -22) * mm, "end": v(-18.25, -22) * mm, "construction": true});
            skLineSegment(sketch, "E141.1", {"start": v(18.25, -22) * mm, "end": v(18.25, -58.5) * mm, "construction": true});
            skLineSegment(sketch, "E141.2", {"start": v(18.25, -58.5) * mm, "end": v(-18.25, -58.5) * mm, "construction": true});
            skLineSegment(sketch, "E141.3", {"start": v(-18.25, -22) * mm, "end": v(-18.25, -58.5) * mm, "construction": true});
            skLineSegment(sketch, "E142", {"start": v(-7.5, -54.75) * mm, "end": v(-7.5, -58.5) * mm});
            skLineSegment(sketch, "E143", {"start": v(7.5, -54.75) * mm, "end": v(7.5, -58.5) * mm});
            skLineSegment(sketch, "E144", {"start": v(-7.5, -58.5) * mm, "end": v(7.5, -58.5) * mm});
            skLineSegment(sketch, "E145.0", {"start": v(-13.75, -31) * mm, "end": v(-13.75, -58.5) * mm, "construction": true});
            skLineSegment(sketch, "E145.1", {"start": v(13.75, -31) * mm, "end": v(-13.75, -31) * mm, "construction": true});
            skLineSegment(sketch, "E145.2", {"start": v(13.75, -31) * mm, "end": v(13.75, -58.5) * mm, "construction": true});
            skLineSegment(sketch, "E146", {"start": v(-7.5, -34.75) * mm, "end": v(-7.5, -31) * mm});
            skLineSegment(sketch, "E147", {"start": v(7.5, -34.75) * mm, "end": v(7.5, -31) * mm});
            skLineSegment(sketch, "E148", {"start": v(-18.25, -37.25) * mm, "end": v(-18.25, -52.5) * mm});
            skLineSegment(sketch, "E149", {"start": v(18.25, -37.25) * mm, "end": v(18.25, -52.5) * mm});
            skArc(sketch, "E150", {"start": v(-15.25, -28) * mm, "mid": v(-13.13, -27.12) * mm, "end": v(-12.25, -25) * mm});
            skArc(sketch, "E151", {"start": v(12.25, -25) * mm, "mid": v(13.13, -27.12) * mm, "end": v(15.25, -28) * mm});
            skLineSegment(sketch, "E152", {"start": v(-12.25, -25) * mm, "end": v(-12.25, -22) * mm});
            skLineSegment(sketch, "E153", {"start": v(-15.25, -28) * mm, "end": v(-18.25, -28) * mm});
            skLineSegment(sketch, "E154", {"start": v(-15.25, -31.75) * mm, "end": v(-18.25, -31.75) * mm});
            skLineSegment(sketch, "E155", {"start": v(-18.25, -28) * mm, "end": v(-18.25, -31.75) * mm});
            skLineSegment(sketch, "E156", {"start": v(15.25, -28) * mm, "end": v(18.25, -28) * mm});
            skLineSegment(sketch, "E157", {"start": v(12.25, -25) * mm, "end": v(12.25, -22) * mm});
            skLineSegment(sketch, "E158", {"start": v(-12.25, -22) * mm, "end": v(-2.5, -22) * mm});
            skLineSegment(sketch, "E159", {"start": v(-2.5, -22) * mm, "end": v(-2.5, -25) * mm});
            skLineSegment(sketch, "E160", {"start": v(-7.5, -31) * mm, "end": v(7.5, -31) * mm});
            skArc(sketch, "E161", {"start": v(-15.25, -31.75) * mm, "mid": v(-10.48, -29.77) * mm, "end": v(-8.5, -25) * mm});
            skLineSegment(sketch, "E162", {"start": v(-8.5, -25) * mm, "end": v(-2.5, -25) * mm});
            skLineSegment(sketch, "E163.MirrorCS", {"start": v(2.5, -22) * mm, "end": v(2.5, -25) * mm});
            skArc(sketch, "E164.MirrorCS", {"start": v(15.25, -31.75) * mm, "mid": v(10.48, -29.77) * mm, "end": v(8.5, -25) * mm});
            skLineSegment(sketch, "E165.MirrorCS", {"start": v(15.25, -31.75) * mm, "end": v(18.25, -31.75) * mm});
            skLineSegment(sketch, "E166", {"start": v(2.5, -25) * mm, "end": v(8.5, -25) * mm});
            skLineSegment(sketch, "E167", {"start": v(2.5, -22) * mm, "end": v(12.25, -22) * mm});
            skLineSegment(sketch, "E168", {"start": v(18.25, -31.75) * mm, "end": v(18.25, -28) * mm});
            skLineSegment(sketch, "E169", {"start": v(-18.25, -52.5) * mm, "end": v(-15.25, -52.5) * mm});
            skLineSegment(sketch, "E170", {"start": v(18.25, -52.5) * mm, "end": v(15.25, -52.5) * mm});
            skLineSegment(sketch, "E171", {"start": v(-10, -52.25) * mm, "end": v(-13.75, -52.25) * mm});
            skLineSegment(sketch, "E172", {"start": v(-13.75, -52.25) * mm, "end": v(-15.25, -52.5) * mm});
            skLineSegment(sketch, "E173", {"start": v(10, -52.25) * mm, "end": v(13.75, -52.25) * mm});
            skLineSegment(sketch, "E174", {"start": v(13.75, -52.25) * mm, "end": v(15.25, -52.5) * mm});
            skLineSegment(sketch, "E175", {"start": v(-10, -37.25) * mm, "end": v(-13.75, -37.25) * mm});
            skLineSegment(sketch, "E176", {"start": v(10, -37.25) * mm, "end": v(13.75, -37.25) * mm});
            skLineSegment(sketch, "E177", {"start": v(-13.75, -37.25) * mm, "end": v(-18.25, -37.25) * mm});
            skLineSegment(sketch, "E178", {"start": v(13.75, -37.25) * mm, "end": v(18.25, -37.25) * mm});
            skLineSegment(sketch, "E179", {"start": v(-15.25, 15.25) * mm, "end": v(15.25, -15.25) * mm, "construction": true});
            skLineSegment(sketch, "E180", {"start": v(15.25, 15.25) * mm, "end": v(-15.25, -15.25) * mm, "construction": true});
            skLineSegment(sketch, "E181", {"start": v(-14.66, 10.42) * mm, "end": v(-5.66, 1.41) * mm});
            skLineSegment(sketch, "E182", {"start": v(-5.66, -1.41) * mm, "end": v(-14.66, -10.42) * mm});
            skLineSegment(sketch, "E183", {"start": v(-7.6, 11.84) * mm, "end": v(-1.41, 5.66) * mm});
            skLineSegment(sketch, "E184", {"start": v(1.41, 5.66) * mm, "end": v(7.6, 11.84) * mm});
            skLineSegment(sketch, "E185", {"start": v(-6.18, 15.25) * mm, "end": v(6.18, 15.25) * mm});
            skLineSegment(sketch, "E186", {"start": v(-16.08, 11) * mm, "end": v(-18, 11) * mm});
            skLineSegment(sketch, "E187", {"start": v(-20, 9) * mm, "end": v(-20, -9) * mm});
            skLineSegment(sketch, "E188", {"start": v(-18, -11) * mm, "end": v(-16.08, -11) * mm});
            skLineSegment(sketch, "E189.MirrorCS", {"start": v(14.66, 10.42) * mm, "end": v(5.66, 1.41) * mm});
            skLineSegment(sketch, "E190.MirrorCS", {"start": v(5.66, -1.41) * mm, "end": v(14.66, -10.42) * mm});
            skLineSegment(sketch, "E191.MirrorCS", {"start": v(16.08, 11) * mm, "end": v(18, 11) * mm});
            skLineSegment(sketch, "E192.MirrorCS", {"start": v(18, -11) * mm, "end": v(16.08, -11) * mm});
            skLineSegment(sketch, "E193.MirrorCS", {"start": v(20, 9) * mm, "end": v(20, -9) * mm});
            skLineSegment(sketch, "E194.MirrorCS", {"start": v(1.41, -5.66) * mm, "end": v(7.6, -11.84) * mm});
            skLineSegment(sketch, "E195.MirrorCS", {"start": v(-7.6, -11.84) * mm, "end": v(-1.41, -5.66) * mm});
            skLineSegment(sketch, "E196.MirrorCS", {"start": v(-6.18, -15.25) * mm, "end": v(6.18, -15.25) * mm});
            skPoint(sketch, "E197.visualSharp", {"position": v(-11, 15.25) * mm});
            skArc(sketch, "E197.filletArc", {"start": v(-6.18, 15.25) * mm, "mid": v(-8.03, 14.02) * mm, "end": v(-7.6, 11.84) * mm});
            skPoint(sketch, "E198.visualSharp", {"position": v(11, 15.25) * mm});
            skArc(sketch, "E198.filletArc", {"start": v(7.6, 11.84) * mm, "mid": v(8.03, 14.02) * mm, "end": v(6.18, 15.25) * mm});
            skPoint(sketch, "E199.visualSharp", {"position": v(-20, 11) * mm});
            skArc(sketch, "E199.filletArc", {"start": v(-18, 11) * mm, "mid": v(-19.41, 10.42) * mm, "end": v(-20, 9) * mm});
            skPoint(sketch, "E200.visualSharp", {"position": v(-15.25, 11) * mm});
            skArc(sketch, "E200.filletArc", {"start": v(-14.66, 10.42) * mm, "mid": v(-15.31, 10.86) * mm, "end": v(-16.08, 11) * mm});
            skPoint(sketch, "E201.visualSharp", {"position": v(-20, -11) * mm});
            skArc(sketch, "E201.filletArc", {"start": v(-20, -9) * mm, "mid": v(-19.41, -10.42) * mm, "end": v(-18, -11) * mm});
            skPoint(sketch, "E202.visualSharp", {"position": v(-15.25, -11) * mm});
            skArc(sketch, "E202.filletArc", {"start": v(-16.08, -11) * mm, "mid": v(-15.31, -10.86) * mm, "end": v(-14.66, -10.42) * mm});
            skPoint(sketch, "E203.visualSharp", {"position": v(-4.24, 0) * mm});
            skArc(sketch, "E203.filletArc", {"start": v(-5.66, -1.41) * mm, "mid": v(-5.07, 0) * mm, "end": v(-5.66, 1.41) * mm});
            skPoint(sketch, "E204.visualSharp", {"position": v(0, 4.24) * mm});
            skArc(sketch, "E204.filletArc", {"start": v(-1.41, 5.66) * mm, "mid": v(0, 5.07) * mm, "end": v(1.41, 5.66) * mm});
            skPoint(sketch, "E205.visualSharp", {"position": v(-11, -15.25) * mm});
            skArc(sketch, "E205.filletArc", {"start": v(-7.6, -11.84) * mm, "mid": v(-8.03, -14.02) * mm, "end": v(-6.18, -15.25) * mm});
            skPoint(sketch, "E206.visualSharp", {"position": v(0, -4.24) * mm});
            skArc(sketch, "E206.filletArc", {"start": v(1.41, -5.66) * mm, "mid": v(0, -5.07) * mm, "end": v(-1.41, -5.66) * mm});
            skPoint(sketch, "E207.visualSharp", {"position": v(11, -15.25) * mm});
            skArc(sketch, "E207.filletArc", {"start": v(6.18, -15.25) * mm, "mid": v(8.03, -14.02) * mm, "end": v(7.6, -11.84) * mm});
            skPoint(sketch, "E208.visualSharp", {"position": v(4.24, 0) * mm});
            skArc(sketch, "E208.filletArc", {"start": v(5.66, 1.41) * mm, "mid": v(5.07, 0) * mm, "end": v(5.66, -1.41) * mm});
            skPoint(sketch, "E209.visualSharp", {"position": v(20, 11) * mm});
            skArc(sketch, "E209.filletArc", {"start": v(20, 9) * mm, "mid": v(19.41, 10.42) * mm, "end": v(18, 11) * mm});
            skPoint(sketch, "E210.visualSharp", {"position": v(15.25, 11) * mm});
            skArc(sketch, "E210.filletArc", {"start": v(16.08, 11) * mm, "mid": v(15.31, 10.86) * mm, "end": v(14.66, 10.42) * mm});
            skPoint(sketch, "E211.visualSharp", {"position": v(15.25, -11) * mm});
            skArc(sketch, "E211.filletArc", {"start": v(14.66, -10.42) * mm, "mid": v(15.31, -10.86) * mm, "end": v(16.08, -11) * mm});
            skPoint(sketch, "E212.visualSharp", {"position": v(20, -11) * mm});
            skArc(sketch, "E212.filletArc", {"start": v(18, -11) * mm, "mid": v(19.41, -10.42) * mm, "end": v(20, -9) * mm});
            skCircle(sketch, "E213", {"center": v(0, 0) * mm, "radius": 2.25 * mm});
            skSolve(sketch);
        }
        {
            var Q0;
            Q0 = qSketchRegion(id + "F10", true);
            extrude(context, id + "F11", {"entities" : qUnion([Q0]), "operationType" : NewBodyOperationType.REMOVE, "endBound" : BoundingType.THROUGH_ALL, "oppositeDirection" : true, "depth" : 25 * mm, "offsetDistance" : 25 * mm});
        }
        {
            var Q0;
            Q0=makeQuery(id+"F11.boolean.opBoolean","COPY",EDGE,{"derivedFrom":makeQuery(id+"F11.opExtrude","SWEPT_EDGE",EDGE,{"disambiguationData":[OSD([sQuery(id+"F10.wireOp",EDGE,"E157"),sQuery(id+"F10.wireOp",EDGE,"E167")])]})});
            var Q1;
            Q1=makeQuery(id+"F11.boolean.opBoolean","COPY",EDGE,{"derivedFrom":makeQuery(id+"F11.opExtrude","SWEPT_EDGE",EDGE,{"disambiguationData":[OSD([sQuery(id+"F10.wireOp",EDGE,"E156"),sQuery(id+"F10.wireOp",EDGE,"E168")])]})});
            var Q2;
            Q2=makeQuery(id+"F11.boolean.opBoolean","COPY",EDGE,{"derivedFrom":makeQuery(id+"F11.opExtrude","SWEPT_EDGE",EDGE,{"disambiguationData":[OSD([sQuery(id+"F10.wireOp",EDGE,"E149"),sQuery(id+"F10.wireOp",EDGE,"E170")])]})});
            var Q3;
            Q3=makeQuery(id+"F11.boolean.opBoolean","COPY",EDGE,{"derivedFrom":makeQuery(id+"F11.opExtrude","SWEPT_EDGE",EDGE,{"disambiguationData":[OSD([sQuery(id+"F10.wireOp",EDGE,"E165.MirrorCS"),sQuery(id+"F10.wireOp",EDGE,"E168")])]})});
            var Q4;
            Q4=makeQuery(id+"F11.boolean.opBoolean","COPY",EDGE,{"derivedFrom":makeQuery(id+"F11.opExtrude","SWEPT_EDGE",EDGE,{"disambiguationData":[OSD([sQuery(id+"F10.wireOp",EDGE,"E149"),sQuery(id+"F10.wireOp",EDGE,"E178")])]})});
            var Q5;
            Q5=makeQuery(id+"F11.boolean.opBoolean","COPY",EDGE,{"derivedFrom":makeQuery(id+"F11.opExtrude","SWEPT_EDGE",EDGE,{"disambiguationData":[OSD([sQuery(id+"F10.wireOp",EDGE,"E147"),sQuery(id+"F10.wireOp",EDGE,"E160")])]})});
            var Q6;
            Q6=makeQuery(id+"F11.boolean.opBoolean","COPY",EDGE,{"derivedFrom":makeQuery(id+"F11.opExtrude","SWEPT_EDGE",EDGE,{"disambiguationData":[OSD([sQuery(id+"F10.wireOp",EDGE,"E143"),sQuery(id+"F10.wireOp",EDGE,"E144")])]})});
            var Q7;
            Q7=makeQuery(id+"F11.boolean.opBoolean","COPY",EDGE,{"derivedFrom":makeQuery(id+"F11.opExtrude","SWEPT_EDGE",EDGE,{"disambiguationData":[OSD([sQuery(id+"F10.wireOp",EDGE,"E163.MirrorCS"),sQuery(id+"F10.wireOp",EDGE,"E167")])]})});
            var Q8;
            Q8=makeQuery(id+"F11.boolean.opBoolean","COPY",EDGE,{"derivedFrom":makeQuery(id+"F11.opExtrude","SWEPT_EDGE",EDGE,{"disambiguationData":[OSD([sQuery(id+"F10.wireOp",EDGE,"E163.MirrorCS"),sQuery(id+"F10.wireOp",EDGE,"E166")])]})});
            var Q9;
            Q9=makeQuery(id+"F11.boolean.opBoolean","COPY",EDGE,{"derivedFrom":makeQuery(id+"F11.opExtrude","SWEPT_EDGE",EDGE,{"disambiguationData":[OSD([sQuery(id+"F10.wireOp",EDGE,"E164.MirrorCS"),sQuery(id+"F10.wireOp",EDGE,"E166")])]})});
            var Q10;
            Q10=makeQuery(id+"F11.boolean.opBoolean","COPY",EDGE,{"derivedFrom":makeQuery(id+"F11.opExtrude","SWEPT_EDGE",EDGE,{"disambiguationData":[OSD([sQuery(id+"F10.wireOp",EDGE,"E142"),sQuery(id+"F10.wireOp",EDGE,"E144")])]})});
            var Q11;
            Q11=makeQuery(id+"F11.boolean.opBoolean","COPY",EDGE,{"derivedFrom":makeQuery(id+"F11.opExtrude","SWEPT_EDGE",EDGE,{"disambiguationData":[OSD([sQuery(id+"F10.wireOp",EDGE,"E148"),sQuery(id+"F10.wireOp",EDGE,"E169")])]})});
            var Q12;
            Q12=makeQuery(id+"F11.boolean.opBoolean","COPY",EDGE,{"derivedFrom":makeQuery(id+"F11.opExtrude","SWEPT_EDGE",EDGE,{"disambiguationData":[OSD([sQuery(id+"F10.wireOp",EDGE,"E154"),sQuery(id+"F10.wireOp",EDGE,"E155")])]})});
            var Q13;
            Q13=makeQuery(id+"F11.boolean.opBoolean","COPY",EDGE,{"derivedFrom":makeQuery(id+"F11.opExtrude","SWEPT_EDGE",EDGE,{"disambiguationData":[OSD([sQuery(id+"F10.wireOp",EDGE,"E161"),sQuery(id+"F10.wireOp",EDGE,"E162")])]})});
            var Q14;
            Q14=makeQuery(id+"F11.boolean.opBoolean","COPY",EDGE,{"derivedFrom":makeQuery(id+"F11.opExtrude","SWEPT_EDGE",EDGE,{"disambiguationData":[OSD([sQuery(id+"F10.wireOp",EDGE,"E146"),sQuery(id+"F10.wireOp",EDGE,"E160")])]})});
            var Q15;
            Q15=makeQuery(id+"F11.boolean.opBoolean","COPY",EDGE,{"derivedFrom":makeQuery(id+"F11.opExtrude","SWEPT_EDGE",EDGE,{"disambiguationData":[OSD([sQuery(id+"F10.wireOp",EDGE,"E153"),sQuery(id+"F10.wireOp",EDGE,"E155")])]})});
            var Q16;
            Q16=makeQuery(id+"F11.boolean.opBoolean","COPY",EDGE,{"derivedFrom":makeQuery(id+"F11.opExtrude","SWEPT_EDGE",EDGE,{"disambiguationData":[OSD([sQuery(id+"F10.wireOp",EDGE,"E152"),sQuery(id+"F10.wireOp",EDGE,"E158")])]})});
            var Q17;
            Q17=makeQuery(id+"F11.boolean.opBoolean","COPY",EDGE,{"derivedFrom":makeQuery(id+"F11.opExtrude","SWEPT_EDGE",EDGE,{"disambiguationData":[OSD([sQuery(id+"F10.wireOp",EDGE,"E158"),sQuery(id+"F10.wireOp",EDGE,"E159")])]})});
            var Q18;
            Q18=makeQuery(id+"F11.boolean.opBoolean","COPY",EDGE,{"derivedFrom":makeQuery(id+"F11.opExtrude","SWEPT_EDGE",EDGE,{"disambiguationData":[OSD([sQuery(id+"F10.wireOp",EDGE,"E159"),sQuery(id+"F10.wireOp",EDGE,"E162")])]})});
            var Q19;
            Q19=makeQuery(id+"F11.boolean.opBoolean","COPY",EDGE,{"derivedFrom":makeQuery(id+"F11.opExtrude","SWEPT_EDGE",EDGE,{"disambiguationData":[OSD([sQuery(id+"F10.wireOp",EDGE,"E148"),sQuery(id+"F10.wireOp",EDGE,"E177")])]})});
            fillet(context, id + "F12", {"entities" : qUnion([Q0, Q1, Q2, Q3, Q4, Q5, Q6, Q7, Q8, Q9, Q10, Q11, Q12, Q13, Q14, Q15, Q16, Q17, Q18, Q19]), "radius" : 1 * mm, "allowEdgeOverflow" : false});
        }
        {
            var Q0;
            Q0=qCreatedBy(makeId("Top.planeOp"),FACE);
            var sketch = newSketch(context, id + "F13", { "sketchPlane" : qUnion([Q0])});
            skLineSegment(sketch, "E214.0.0", {"start": v(-20, 9) * mm, "end": v(-20, -9) * mm});
            skArc(sketch, "E214.0.1", {"start": v(-20, -9) * mm, "mid": v(-19.41, -10.42) * mm, "end": v(-18, -11) * mm});
            skLineSegment(sketch, "E214.0.2", {"start": v(-18, -11) * mm, "end": v(-16.08, -11) * mm});
            skArc(sketch, "E214.0.3", {"start": v(-16.08, -11) * mm, "mid": v(-15.31, -10.86) * mm, "end": v(-14.66, -10.42) * mm});
            skLineSegment(sketch, "E214.0.4", {"start": v(-14.66, -10.42) * mm, "end": v(-5.66, -1.41) * mm});
            skArc(sketch, "E214.0.5", {"start": v(-5.66, -1.41) * mm, "mid": v(-5.07, 0) * mm, "end": v(-5.66, 1.41) * mm});
            skLineSegment(sketch, "E214.0.6", {"start": v(-5.66, 1.41) * mm, "end": v(-14.66, 10.42) * mm});
            skArc(sketch, "E214.0.7", {"start": v(-14.66, 10.42) * mm, "mid": v(-15.31, 10.86) * mm, "end": v(-16.08, 11) * mm});
            skLineSegment(sketch, "E214.0.8", {"start": v(-16.08, 11) * mm, "end": v(-18, 11) * mm});
            skArc(sketch, "E214.0.9", {"start": v(-18, 11) * mm, "mid": v(-19.41, 10.42) * mm, "end": v(-20, 9) * mm});
            skLineSegment(sketch, "E215.0.0", {"start": v(1.41, 5.66) * mm, "end": v(7.6, 11.84) * mm});
            skArc(sketch, "E215.0.1", {"start": v(7.6, 11.84) * mm, "mid": v(8.03, 14.02) * mm, "end": v(6.18, 15.25) * mm});
            skLineSegment(sketch, "E215.0.2", {"start": v(6.18, 15.25) * mm, "end": v(-6.18, 15.25) * mm});
            skArc(sketch, "E215.0.3", {"start": v(-6.18, 15.25) * mm, "mid": v(-8.03, 14.02) * mm, "end": v(-7.6, 11.84) * mm});
            skLineSegment(sketch, "E215.0.4", {"start": v(-7.6, 11.84) * mm, "end": v(-1.41, 5.66) * mm});
            skArc(sketch, "E215.0.5", {"start": v(-1.41, 5.66) * mm, "mid": v(0, 5.07) * mm, "end": v(1.41, 5.66) * mm});
            skLineSegment(sketch, "E216.0.0", {"start": v(-1.41, -5.66) * mm, "end": v(-7.6, -11.84) * mm});
            skArc(sketch, "E216.0.1", {"start": v(-7.6, -11.84) * mm, "mid": v(-8.03, -14.02) * mm, "end": v(-6.18, -15.25) * mm});
            skLineSegment(sketch, "E216.0.2", {"start": v(-6.18, -15.25) * mm, "end": v(6.18, -15.25) * mm});
            skArc(sketch, "E216.0.3", {"start": v(6.18, -15.25) * mm, "mid": v(8.03, -14.02) * mm, "end": v(7.6, -11.84) * mm});
            skLineSegment(sketch, "E216.0.4", {"start": v(7.6, -11.84) * mm, "end": v(1.41, -5.66) * mm});
            skArc(sketch, "E216.0.5", {"start": v(1.41, -5.66) * mm, "mid": v(0, -5.07) * mm, "end": v(-1.41, -5.66) * mm});
            skLineSegment(sketch, "E217.0.0", {"start": v(16.08, -11) * mm, "end": v(18, -11) * mm});
            skArc(sketch, "E217.0.1", {"start": v(18, -11) * mm, "mid": v(19.41, -10.42) * mm, "end": v(20, -9) * mm});
            skLineSegment(sketch, "E217.0.2", {"start": v(20, -9) * mm, "end": v(20, 9) * mm});
            skArc(sketch, "E217.0.3", {"start": v(20, 9) * mm, "mid": v(19.41, 10.42) * mm, "end": v(18, 11) * mm});
            skLineSegment(sketch, "E217.0.4", {"start": v(18, 11) * mm, "end": v(16.08, 11) * mm});
            skArc(sketch, "E217.0.5", {"start": v(16.08, 11) * mm, "mid": v(15.31, 10.86) * mm, "end": v(14.66, 10.42) * mm});
            skLineSegment(sketch, "E217.0.6", {"start": v(14.66, 10.42) * mm, "end": v(5.66, 1.41) * mm});
            skArc(sketch, "E217.0.7", {"start": v(5.66, 1.41) * mm, "mid": v(5.07, 0) * mm, "end": v(5.66, -1.41) * mm});
            skLineSegment(sketch, "E217.0.8", {"start": v(5.66, -1.41) * mm, "end": v(14.66, -10.42) * mm});
            skArc(sketch, "E217.0.9", {"start": v(14.66, -10.42) * mm, "mid": v(15.31, -10.86) * mm, "end": v(16.08, -11) * mm});
            skCircle(sketch, "E218", {"center": v(0, 0) * mm, "radius": 1.55 * mm});
            skSolve(sketch);
        }
        {
            var Q0;
            Q0 = qSketchRegion(id + "F13", true);
            extrude(context, id + "F14", {"entities" : qUnion([Q0]), "operationType" : NewBodyOperationType.REMOVE, "endBound" : BoundingType.THROUGH_ALL, "depth" : 25 * mm, "offsetDistance" : 25 * mm});
        }
        {
            var Q0;
            Q0 = qSketchRegion(id + "F13", true);
            extrude(context, id + "F15", {"entities" : qUnion([Q0]), "operationType" : NewBodyOperationType.REMOVE, "endBound" : BoundingType.THROUGH_ALL, "depth" : 25 * mm, "offsetDistance" : 25 * mm});
        }
        {
            var Q0;
            Q0=qCreatedBy(makeId("Top.planeOp"),FACE);
            var sketch = newSketch(context, id + "F16", { "sketchPlane" : qUnion([Q0])});
            skLineSegment(sketch, "E219", {"start": v(-17.54, 20.84) * mm, "end": v(-4, 20.84) * mm, "construction": true});
            skLineSegment(sketch, "E220.MirrorCS", {"start": v(17.54, 20.84) * mm, "end": v(4, 20.84) * mm, "construction": true});
            skLineSegment(sketch, "E221.MirrorCS", {"start": v(-17.54, -20.84) * mm, "end": v(-4, -20.84) * mm, "construction": true});
            skLineSegment(sketch, "E222.MirrorCS", {"start": v(17.54, -20.84) * mm, "end": v(4, -20.84) * mm, "construction": true});
            skArc(sketch, "E223.0.startCap", {"start": v(-17.54, 19.6) * mm, "mid": v(-18.8, 20.84) * mm, "end": v(-17.54, 22.1) * mm});
            skArc(sketch, "E223.0.endCap", {"start": v(-4, 22.1) * mm, "mid": v(-2.75, 20.84) * mm, "end": v(-4, 19.6) * mm});
            skLineSegment(sketch, "E223.0.left", {"start": v(-17.54, 22.1) * mm, "end": v(-4, 22.1) * mm});
            skLineSegment(sketch, "E223.0.right", {"start": v(-17.54, 19.6) * mm, "end": v(-4, 19.6) * mm});
            skArc(sketch, "E224.0.startCap", {"start": v(17.54, 22.1) * mm, "mid": v(18.8, 20.84) * mm, "end": v(17.54, 19.6) * mm});
            skArc(sketch, "E224.0.endCap", {"start": v(4, 19.6) * mm, "mid": v(2.75, 20.84) * mm, "end": v(4, 22.1) * mm});
            skLineSegment(sketch, "E224.0.left", {"start": v(17.54, 19.6) * mm, "end": v(4, 19.6) * mm});
            skLineSegment(sketch, "E224.0.right", {"start": v(17.54, 22.1) * mm, "end": v(4, 22.1) * mm});
            skArc(sketch, "E225.0.startCap", {"start": v(-17.54, -22.1) * mm, "mid": v(-18.8, -20.84) * mm, "end": v(-17.54, -19.6) * mm});
            skArc(sketch, "E225.0.endCap", {"start": v(-4, -19.6) * mm, "mid": v(-2.75, -20.84) * mm, "end": v(-4, -22.1) * mm});
            skLineSegment(sketch, "E225.0.left", {"start": v(-17.54, -19.6) * mm, "end": v(-4, -19.6) * mm});
            skLineSegment(sketch, "E225.0.right", {"start": v(-17.54, -22.1) * mm, "end": v(-4, -22.1) * mm});
            skArc(sketch, "E226.0.startCap", {"start": v(17.54, -19.6) * mm, "mid": v(18.8, -20.84) * mm, "end": v(17.54, -22.1) * mm});
            skArc(sketch, "E226.0.endCap", {"start": v(4, -22.1) * mm, "mid": v(2.75, -20.84) * mm, "end": v(4, -19.6) * mm});
            skLineSegment(sketch, "E226.0.left", {"start": v(17.54, -22.1) * mm, "end": v(4, -22.1) * mm});
            skLineSegment(sketch, "E226.0.right", {"start": v(17.54, -19.6) * mm, "end": v(4, -19.6) * mm});
            skSolve(sketch);
        }
        {
            var Q0;
            Q0 = qSketchRegion(id + "F16", true);
            extrude(context, id + "F17", {"entities" : qUnion([Q0]), "operationType" : NewBodyOperationType.REMOVE, "endBound" : BoundingType.THROUGH_ALL, "depth" : 25 * mm, "offsetDistance" : 25 * mm});
        }
        {
            var Q0;
            Q0=qCreatedBy(makeId("Top.planeOp"),FACE);
            var sketch = newSketch(context, id + "F18", { "sketchPlane" : qUnion([Q0])});
            skLineSegment(sketch, "E227.bottom", {"start": v(22.5, 39.35) * mm, "end": v(-22.5, 39.35) * mm, "construction": true});
            skLineSegment(sketch, "E227.top", {"start": v(22.5, 18.5) * mm, "end": v(-22.5, 18.5) * mm, "construction": true});
            skLineSegment(sketch, "E227.left", {"start": v(22.5, 39.35) * mm, "end": v(22.5, 18.5) * mm, "construction": true});
            skLineSegment(sketch, "E227.right", {"start": v(-22.5, 39.35) * mm, "end": v(-22.5, 18.5) * mm, "construction": true});
            skPoint(sketch, "E227.middle", {"position": v(0, 28.92) * mm});
            skLineSegment(sketch, "E228", {"start": v(-22.5, 39.35) * mm, "end": v(0, 28.92) * mm, "construction": true});
            skLineSegment(sketch, "E229", {"start": v(22.5, 39.35) * mm, "end": v(0, 28.92) * mm, "construction": true});
            skLineSegment(sketch, "E230", {"start": v(0, 28.92) * mm, "end": v(22.5, 18.5) * mm, "construction": true});
            skLineSegment(sketch, "E231", {"start": v(0, 28.92) * mm, "end": v(-22.5, 18.5) * mm, "construction": true});
            skLineSegment(sketch, "E232.0", {"start": v(-21, 32.3) * mm, "end": v(-21, 25.54) * mm});
            skLineSegment(sketch, "E232.1", {"start": v(-16.74, 35.03) * mm, "end": v(-7.48, 30.74) * mm});
            skLineSegment(sketch, "E232.2", {"start": v(-7.48, 27.1) * mm, "end": v(-16.74, 22.82) * mm});
            skLineSegment(sketch, "E233.0", {"start": v(8.9, 38.35) * mm, "end": v(-8.9, 38.35) * mm});
            skLineSegment(sketch, "E233.1", {"start": v(9.73, 34.53) * mm, "end": v(1.26, 30.6) * mm});
            skLineSegment(sketch, "E233.2", {"start": v(-9.73, 34.53) * mm, "end": v(-1.26, 30.6) * mm});
            skLineSegment(sketch, "E234.0", {"start": v(8.9, 19.5) * mm, "end": v(-8.9, 19.5) * mm});
            skLineSegment(sketch, "E234.1", {"start": v(1.26, 27.23) * mm, "end": v(9.73, 23.3) * mm});
            skLineSegment(sketch, "E234.2", {"start": v(-1.26, 27.23) * mm, "end": v(-9.73, 23.3) * mm});
            skLineSegment(sketch, "E235.0", {"start": v(21, 32.3) * mm, "end": v(21, 25.54) * mm});
            skLineSegment(sketch, "E235.1", {"start": v(16.74, 35.03) * mm, "end": v(7.48, 30.74) * mm});
            skLineSegment(sketch, "E235.2", {"start": v(7.48, 27.1) * mm, "end": v(16.74, 22.82) * mm});
            skPoint(sketch, "E236.visualSharp", {"position": v(-21, 37) * mm});
            skArc(sketch, "E236.filletArc", {"start": v(-16.74, 35.03) * mm, "mid": v(-19.61, 34.83) * mm, "end": v(-21, 32.3) * mm});
            skPoint(sketch, "E237.visualSharp", {"position": v(-21, 20.84) * mm});
            skArc(sketch, "E237.filletArc", {"start": v(-21, 25.54) * mm, "mid": v(-19.61, 23.01) * mm, "end": v(-16.74, 22.82) * mm});
            skPoint(sketch, "E238.visualSharp", {"position": v(-3.57, 28.92) * mm});
            skArc(sketch, "E238.filletArc", {"start": v(-7.48, 27.1) * mm, "mid": v(-6.32, 28.92) * mm, "end": v(-7.48, 30.74) * mm});
            skPoint(sketch, "E239.visualSharp", {"position": v(-17.96, 19.5) * mm});
            skArc(sketch, "E239.filletArc", {"start": v(-9.73, 23.3) * mm, "mid": v(-10.84, 21.06) * mm, "end": v(-8.9, 19.5) * mm});
            skPoint(sketch, "E240.visualSharp", {"position": v(17.96, 19.5) * mm});
            skArc(sketch, "E240.filletArc", {"start": v(8.9, 19.5) * mm, "mid": v(10.84, 21.06) * mm, "end": v(9.73, 23.3) * mm});
            skPoint(sketch, "E241.visualSharp", {"position": v(-17.96, 38.35) * mm});
            skArc(sketch, "E241.filletArc", {"start": v(-8.9, 38.35) * mm, "mid": v(-10.84, 36.78) * mm, "end": v(-9.73, 34.53) * mm});
            skPoint(sketch, "E242.visualSharp", {"position": v(17.96, 38.35) * mm});
            skArc(sketch, "E242.filletArc", {"start": v(9.73, 34.53) * mm, "mid": v(10.84, 36.78) * mm, "end": v(8.9, 38.35) * mm});
            skPoint(sketch, "E243.visualSharp", {"position": v(0, 30.02) * mm});
            skArc(sketch, "E243.filletArc", {"start": v(-1.26, 30.6) * mm, "mid": v(0, 30.33) * mm, "end": v(1.26, 30.6) * mm});
            skPoint(sketch, "E244.visualSharp", {"position": v(0, 27.82) * mm});
            skArc(sketch, "E244.filletArc", {"start": v(1.26, 27.23) * mm, "mid": v(0, 27.51) * mm, "end": v(-1.26, 27.23) * mm});
            skPoint(sketch, "E245.visualSharp", {"position": v(3.57, 28.92) * mm});
            skArc(sketch, "E245.filletArc", {"start": v(7.48, 30.74) * mm, "mid": v(6.32, 28.92) * mm, "end": v(7.48, 27.1) * mm});
            skPoint(sketch, "E246.visualSharp", {"position": v(21, 37) * mm});
            skArc(sketch, "E246.filletArc", {"start": v(21, 32.3) * mm, "mid": v(19.61, 34.83) * mm, "end": v(16.74, 35.03) * mm});
            skPoint(sketch, "E247.visualSharp", {"position": v(21, 20.84) * mm});
            skArc(sketch, "E247.filletArc", {"start": v(16.74, 22.82) * mm, "mid": v(19.61, 23.01) * mm, "end": v(21, 25.54) * mm});
            skLineSegment(sketch, "E248.MirrorCS", {"start": v(-21, -32.3) * mm, "end": v(-21, -25.54) * mm});
            skArc(sketch, "E249.MirrorCS", {"start": v(-16.74, -35.03) * mm, "mid": v(-19.61, -34.83) * mm, "end": v(-21, -32.3) * mm});
            skLineSegment(sketch, "E250.MirrorCS", {"start": v(-16.74, -35.03) * mm, "end": v(-7.48, -30.74) * mm});
            skArc(sketch, "E251.MirrorCS", {"start": v(-7.48, -27.1) * mm, "mid": v(-6.32, -28.92) * mm, "end": v(-7.48, -30.74) * mm});
            skLineSegment(sketch, "E252.MirrorCS", {"start": v(-7.48, -27.1) * mm, "end": v(-16.74, -22.82) * mm});
            skArc(sketch, "E253.MirrorCS", {"start": v(-9.73, -23.3) * mm, "mid": v(-10.84, -21.06) * mm, "end": v(-8.9, -19.5) * mm});
            skLineSegment(sketch, "E254.MirrorCS", {"start": v(-1.26, -27.23) * mm, "end": v(-9.73, -23.3) * mm});
            skLineSegment(sketch, "E255.MirrorCS", {"start": v(1.26, -27.23) * mm, "end": v(9.73, -23.3) * mm});
            skLineSegment(sketch, "E256.MirrorCS", {"start": v(8.9, -19.5) * mm, "end": v(-8.9, -19.5) * mm});
            skArc(sketch, "E257.MirrorCS", {"start": v(8.9, -19.5) * mm, "mid": v(10.84, -21.06) * mm, "end": v(9.73, -23.3) * mm});
            skArc(sketch, "E258.MirrorCS", {"start": v(1.26, -27.23) * mm, "mid": v(0, -27.51) * mm, "end": v(-1.26, -27.23) * mm});
            skArc(sketch, "E259.MirrorCS", {"start": v(-1.26, -30.6) * mm, "mid": v(0, -30.33) * mm, "end": v(1.26, -30.6) * mm});
            skLineSegment(sketch, "E260.MirrorCS", {"start": v(-9.73, -34.53) * mm, "end": v(-1.26, -30.6) * mm});
            skLineSegment(sketch, "E261.MirrorCS", {"start": v(9.73, -34.53) * mm, "end": v(1.26, -30.6) * mm});
            skArc(sketch, "E262.MirrorCS", {"start": v(-8.9, -38.35) * mm, "mid": v(-10.84, -36.78) * mm, "end": v(-9.73, -34.53) * mm});
            skArc(sketch, "E263.MirrorCS", {"start": v(9.73, -34.53) * mm, "mid": v(10.84, -36.78) * mm, "end": v(8.9, -38.35) * mm});
            skLineSegment(sketch, "E264.MirrorCS", {"start": v(8.9, -38.35) * mm, "end": v(-8.9, -38.35) * mm});
            skArc(sketch, "E265.MirrorCS", {"start": v(7.48, -30.74) * mm, "mid": v(6.32, -28.92) * mm, "end": v(7.48, -27.1) * mm});
            skLineSegment(sketch, "E266.MirrorCS", {"start": v(16.74, -35.03) * mm, "end": v(7.48, -30.74) * mm});
            skArc(sketch, "E267.MirrorCS", {"start": v(21, -32.3) * mm, "mid": v(19.61, -34.83) * mm, "end": v(16.74, -35.03) * mm});
            skLineSegment(sketch, "E268.MirrorCS", {"start": v(21, -32.3) * mm, "end": v(21, -25.54) * mm});
            skArc(sketch, "E269.MirrorCS", {"start": v(16.74, -22.82) * mm, "mid": v(19.61, -23.01) * mm, "end": v(21, -25.54) * mm});
            skLineSegment(sketch, "E270.MirrorCS", {"start": v(7.48, -27.1) * mm, "end": v(16.74, -22.82) * mm});
            skArc(sketch, "E271.MirrorCS", {"start": v(-21, -25.54) * mm, "mid": v(-19.61, -23.01) * mm, "end": v(-16.74, -22.82) * mm});
            skSolve(sketch);
        }
        {
            var Q0;
            Q0 = qSketchRegion(id + "F18", true);
            extrude(context, id + "F19", {"entities" : qUnion([Q0]), "operationType" : NewBodyOperationType.REMOVE, "endBound" : BoundingType.THROUGH_ALL, "depth" : 25 * mm, "offsetDistance" : 25 * mm});
        }
        {
            var Q0;
            Q0=makeQuery(id+"F3.opExtrude","CAP_FACE",FACE,{"disambiguationData":[OSD([sQuery(id+"F2.wireOp",EDGE,"E36.0"),sQuery(id+"F2.wireOp",EDGE,"E37.0"),sQuery(id+"F2.wireOp",EDGE,"E38.0"),sQuery(id+"F2.wireOp",EDGE,"E39.0"),sQuery(id+"F2.wireOp",EDGE,"E40.0"),sQuery(id+"F2.wireOp",EDGE,"E41.0"),sQuery(id+"F2.wireOp",EDGE,"E42.0"),sQuery(id+"F2.wireOp",EDGE,"E43.0"),sQuery(id+"F2.wireOp",EDGE,"E44.0"),sQuery(id+"F2.wireOp",EDGE,"E45.0"),sQuery(id+"F2.wireOp",EDGE,"E46.0"),sQuery(id+"F2.wireOp",EDGE,"E47.bottom"),sQuery(id+"F2.wireOp",EDGE,"E47.top"),sQuery(id+"F2.wireOp",EDGE,"E47.left"),sQuery(id+"F2.wireOp",EDGE,"E47.right"),sQuery(id+"F2.wireOp",EDGE,"E48"),sQuery(id+"F2.wireOp",EDGE,"E49"),sQuery(id+"F2.wireOp",EDGE,"E50"),sQuery(id+"F2.wireOp",EDGE,"E51.MirrorCS"),sQuery(id+"F2.wireOp",EDGE,"E52.MirrorCS"),sQuery(id+"F2.wireOp",EDGE,"E53.MirrorCS"),sQuery(id+"F2.wireOp",EDGE,"E54"),sQuery(id+"F2.wireOp",EDGE,"E55.MirrorCS"),sQuery(id+"F2.wireOp",EDGE,"E57"),sQuery(id+"F2.wireOp",EDGE,"E63"),sQuery(id+"F2.wireOp",EDGE,"E65"),sQuery(id+"F2.wireOp",EDGE,"E67"),sQuery(id+"F2.wireOp",EDGE,"E69"),sQuery(id+"F2.wireOp",EDGE,"E72"),sQuery(id+"F2.wireOp",EDGE,"E75"),sQuery(id+"F2.wireOp",EDGE,"E78"),sQuery(id+"F2.wireOp",EDGE,"E79"),sQuery(id+"F2.wireOp",EDGE,"E80")])],"isStart":false});
            var sketch = newSketch(context, id + "F20", { "sketchPlane" : qUnion([Q0])});
            skLineSegment(sketch, "E272.bottom", {"start": v(14.5, 67) * mm, "end": v(-14.5, 67) * mm, "construction": true});
            skLineSegment(sketch, "E272.top", {"start": v(14.5, 17) * mm, "end": v(-14.5, 17) * mm, "construction": true});
            skLineSegment(sketch, "E272.left", {"start": v(14.5, 67) * mm, "end": v(14.5, 17) * mm, "construction": true});
            skLineSegment(sketch, "E272.right", {"start": v(-14.5, 67) * mm, "end": v(-14.5, 17) * mm, "construction": true});
            skPoint(sketch, "E272.middle", {"position": v(0, 42) * mm});
            skLineSegment(sketch, "E273.bottom", {"start": v(5, 37) * mm, "end": v(-5, 37) * mm, "construction": true});
            skLineSegment(sketch, "E273.top", {"start": v(5, 47) * mm, "end": v(-5, 47) * mm, "construction": true});
            skLineSegment(sketch, "E273.left", {"start": v(5, 37) * mm, "end": v(5, 47) * mm, "construction": true});
            skLineSegment(sketch, "E273.right", {"start": v(-5, 37) * mm, "end": v(-5, 47) * mm, "construction": true});
            skLineSegment(sketch, "E274", {"start": v(-5, 47) * mm, "end": v(-5, 57) * mm, "construction": true});
            skLineSegment(sketch, "E275", {"start": v(-5, 37) * mm, "end": v(-5, 27) * mm, "construction": true});
            skLineSegment(sketch, "E276", {"start": v(-5, 27) * mm, "end": v(5, 27) * mm, "construction": true});
            skLineSegment(sketch, "E277", {"start": v(5, 27) * mm, "end": v(5, 37) * mm, "construction": true});
            skLineSegment(sketch, "E278", {"start": v(-5, 57) * mm, "end": v(5, 57) * mm, "construction": true});
            skLineSegment(sketch, "E279", {"start": v(5, 57) * mm, "end": v(5, 47) * mm, "construction": true});
            skCircle(sketch, "E280", {"center": v(5, 47) * mm, "radius": 1 * mm});
            skCircle(sketch, "E281", {"center": v(-5, 47) * mm, "radius": 1 * mm});
            skCircle(sketch, "E282", {"center": v(5, 37) * mm, "radius": 1 * mm});
            skCircle(sketch, "E283", {"center": v(-5, 37) * mm, "radius": 1 * mm});
            skCircle(sketch, "E284", {"center": v(-5, 27) * mm, "radius": 1 * mm});
            skCircle(sketch, "E285", {"center": v(5, 27) * mm, "radius": 1 * mm});
            skCircle(sketch, "E286", {"center": v(20, 58) * mm, "radius": 1.25 * mm});
            skCircle(sketch, "E287", {"center": v(20, 45) * mm, "radius": 1.25 * mm});
            skCircle(sketch, "E288.MirrorC", {"center": v(-20, 58) * mm, "radius": 1.25 * mm});
            skCircle(sketch, "E289.MirrorC", {"center": v(-20, 45) * mm, "radius": 1.25 * mm});
            skLineSegment(sketch, "E290", {"start": v(9, 58) * mm, "end": v(9, 51.5) * mm, "construction": true});
            skLineSegment(sketch, "E291", {"start": v(9, 51.5) * mm, "end": v(0, 51.5) * mm, "construction": true});
            skLineSegment(sketch, "E292.MirrorCS", {"start": v(-9, 58) * mm, "end": v(-9, 51.5) * mm, "construction": true});
            skLineSegment(sketch, "E293.MirrorCS", {"start": v(-9, 51.5) * mm, "end": v(0, 51.5) * mm, "construction": true});
            skLineSegment(sketch, "E294.0", {"start": v(23, 62) * mm, "end": v(-23, 62) * mm, "construction": true});
            skArc(sketch, "E295.0.startCap", {"start": v(8, 58) * mm, "mid": v(9, 59) * mm, "end": v(10, 58) * mm});
            skArc(sketch, "E295.0.endCap", {"start": v(10, 51.5) * mm, "mid": v(9.7, 50.8) * mm, "end": v(9, 50.5) * mm});
            skLineSegment(sketch, "E295.0.left", {"start": v(10, 58) * mm, "end": v(10, 51.5) * mm});
            skLineSegment(sketch, "E295.0.right", {"start": v(8, 58) * mm, "end": v(8, 53.5) * mm});
            skArc(sketch, "E295.1.startCap", {"start": v(10, 51.5) * mm, "mid": v(9.7, 50.8) * mm, "end": v(9, 50.5) * mm});
            skLineSegment(sketch, "E295.1.left", {"start": v(9, 50.5) * mm, "end": v(2.25, 50.5) * mm});
            skLineSegment(sketch, "E295.1.right", {"start": v(7, 52.5) * mm, "end": v(2.25, 52.5) * mm});
            skArc(sketch, "E295.2.startCap", {"start": v(-9, 50.5) * mm, "mid": v(-9.7, 50.8) * mm, "end": v(-10, 51.5) * mm});
            skLineSegment(sketch, "E295.2.left", {"start": v(-7, 52.5) * mm, "end": v(-2.25, 52.5) * mm});
            skLineSegment(sketch, "E295.2.right", {"start": v(-9, 50.5) * mm, "end": v(-2.25, 50.5) * mm});
            skArc(sketch, "E295.3.startCap", {"start": v(-10, 58) * mm, "mid": v(-9, 59) * mm, "end": v(-8, 58) * mm});
            skArc(sketch, "E295.3.endCap", {"start": v(-9, 50.5) * mm, "mid": v(-9.7, 50.8) * mm, "end": v(-10, 51.5) * mm});
            skLineSegment(sketch, "E295.3.left", {"start": v(-8, 58) * mm, "end": v(-8, 53.5) * mm});
            skLineSegment(sketch, "E295.3.right", {"start": v(-10, 58) * mm, "end": v(-10, 51.5) * mm});
            skPoint(sketch, "E296.visualSharp", {"position": v(-8, 52.5) * mm});
            skArc(sketch, "E296.filletArc", {"start": v(-8, 53.5) * mm, "mid": v(-7.7, 52.8) * mm, "end": v(-7, 52.5) * mm});
            skPoint(sketch, "E297.visualSharp", {"position": v(8, 52.5) * mm});
            skArc(sketch, "E297.filletArc", {"start": v(7, 52.5) * mm, "mid": v(7.7, 52.8) * mm, "end": v(8, 53.5) * mm});
            skArc(sketch, "E298", {"start": v(-5, 44.5) * mm, "mid": v(-3.23, 45.23) * mm, "end": v(-2.5, 47) * mm});
            skArc(sketch, "E299", {"start": v(2.5, 47) * mm, "mid": v(3.23, 45.23) * mm, "end": v(5, 44.5) * mm});
            skArc(sketch, "E300", {"start": v(-5, 29.5) * mm, "mid": v(-3.23, 28.77) * mm, "end": v(-2.5, 27) * mm});
            skArc(sketch, "E301", {"start": v(5, 29.5) * mm, "mid": v(3.23, 28.77) * mm, "end": v(2.5, 27) * mm});
            skLineSegment(sketch, "E302", {"start": v(-2.5, 47) * mm, "end": v(-2.5, 48) * mm});
            skLineSegment(sketch, "E303", {"start": v(-2.5, 48) * mm, "end": v(2.5, 48) * mm});
            skLineSegment(sketch, "E304", {"start": v(2.5, 48) * mm, "end": v(2.5, 47) * mm});
            skLineSegment(sketch, "E305", {"start": v(-2.5, 27) * mm, "end": v(-2.5, 26) * mm});
            skLineSegment(sketch, "E306", {"start": v(-2.5, 26) * mm, "end": v(2.5, 26) * mm});
            skLineSegment(sketch, "E307", {"start": v(2.5, 26) * mm, "end": v(2.5, 27) * mm});
            skArc(sketch, "E308", {"start": v(-5, 39.5) * mm, "mid": v(-2.5, 37) * mm, "end": v(-5, 34.5) * mm});
            skArc(sketch, "E309", {"start": v(5, 39.5) * mm, "mid": v(2.5, 37) * mm, "end": v(5, 34.5) * mm});
            skLineSegment(sketch, "E310", {"start": v(-5, 44.5) * mm, "end": v(-6, 44.5) * mm});
            skLineSegment(sketch, "E311", {"start": v(-6, 44.5) * mm, "end": v(-6, 39.5) * mm});
            skLineSegment(sketch, "E312", {"start": v(-6, 39.5) * mm, "end": v(-5, 39.5) * mm});
            skLineSegment(sketch, "E313", {"start": v(5, 44.5) * mm, "end": v(6, 44.5) * mm});
            skLineSegment(sketch, "E314", {"start": v(6, 44.5) * mm, "end": v(6, 39.5) * mm});
            skLineSegment(sketch, "E315", {"start": v(6, 39.5) * mm, "end": v(5, 39.5) * mm});
            skLineSegment(sketch, "E316", {"start": v(-5, 34.5) * mm, "end": v(-6, 34.5) * mm});
            skLineSegment(sketch, "E317", {"start": v(-6, 34.5) * mm, "end": v(-6, 29.5) * mm});
            skLineSegment(sketch, "E318", {"start": v(-6, 29.5) * mm, "end": v(-5, 29.5) * mm});
            skLineSegment(sketch, "E319", {"start": v(5, 34.5) * mm, "end": v(6, 34.5) * mm});
            skLineSegment(sketch, "E320", {"start": v(6, 34.5) * mm, "end": v(6, 29.5) * mm});
            skLineSegment(sketch, "E321", {"start": v(6, 29.5) * mm, "end": v(5, 29.5) * mm});
            skArc(sketch, "E322", {"start": v(-2.25, 52.5) * mm, "mid": v(-1.25, 51.5) * mm, "end": v(-2.25, 50.5) * mm});
            skArc(sketch, "E323.MirrorCS", {"start": v(2.25, 52.5) * mm, "mid": v(1.25, 51.5) * mm, "end": v(2.25, 50.5) * mm});
            skPoint(sketch, "E324.orphan", {"position": v(0, 52.5) * mm});
            skPoint(sketch, "E325.orphan", {"position": v(0, 50.5) * mm});
            skLineSegment(sketch, "E326", {"start": v(-14.5, 32.61) * mm, "end": v(-14.5, 25.61) * mm, "construction": true});
            skArc(sketch, "E327.0.startCap", {"start": v(-16, 32.61) * mm, "mid": v(-14.5, 34.11) * mm, "end": v(-13, 32.61) * mm});
            skArc(sketch, "E327.0.endCap", {"start": v(-13, 25.61) * mm, "mid": v(-14.5, 24.11) * mm, "end": v(-16, 25.61) * mm});
            skLineSegment(sketch, "E327.0.left", {"start": v(-13, 32.61) * mm, "end": v(-13, 25.61) * mm});
            skLineSegment(sketch, "E327.0.right", {"start": v(-16, 32.61) * mm, "end": v(-16, 25.61) * mm});
            skArc(sketch, "E328.MirrorCS", {"start": v(13, 25.61) * mm, "mid": v(14.5, 24.11) * mm, "end": v(16, 25.61) * mm});
            skArc(sketch, "E329.MirrorCS", {"start": v(16, 32.61) * mm, "mid": v(14.5, 34.11) * mm, "end": v(13, 32.61) * mm});
            skLineSegment(sketch, "E330.MirrorCS", {"start": v(16, 32.61) * mm, "end": v(16, 25.61) * mm});
            skLineSegment(sketch, "E331.MirrorCS", {"start": v(13, 32.61) * mm, "end": v(13, 25.61) * mm});
            skPoint(sketch, "E332", {"position": v(-25, 29.11) * mm});
            skPoint(sketch, "E333", {"position": v(-14.5, 29.11) * mm});
            skSolve(sketch);
        }
        {
            var Q0;
            Q0 = qSketchRegion(id + "F20", true);
            extrude(context, id + "F21", {"entities" : qUnion([Q0]), "operationType" : NewBodyOperationType.REMOVE, "endBound" : BoundingType.THROUGH_ALL, "oppositeDirection" : true, "depth" : 25 * mm, "offsetDistance" : 25 * mm});
        }
        {
            var Q0;
            Q0=makeQuery(id+"F21.boolean.opBoolean","COPY",EDGE,{"derivedFrom":makeQuery(id+"F21.opExtrude","SWEPT_EDGE",EDGE,{"disambiguationData":[OSD([sQuery(id+"F20.wireOp",EDGE,"E310"),sQuery(id+"F20.wireOp",EDGE,"E311")])]})});
            var Q1;
            Q1=makeQuery(id+"F21.boolean.opBoolean","COPY",EDGE,{"derivedFrom":makeQuery(id+"F21.opExtrude","SWEPT_EDGE",EDGE,{"disambiguationData":[OSD([sQuery(id+"F20.wireOp",EDGE,"E302"),sQuery(id+"F20.wireOp",EDGE,"E303")])]})});
            var Q2;
            Q2=makeQuery(id+"F21.boolean.opBoolean","COPY",EDGE,{"derivedFrom":makeQuery(id+"F21.opExtrude","SWEPT_EDGE",EDGE,{"disambiguationData":[OSD([sQuery(id+"F20.wireOp",EDGE,"E303"),sQuery(id+"F20.wireOp",EDGE,"E304")])]})});
            var Q3;
            Q3=makeQuery(id+"F21.boolean.opBoolean","COPY",EDGE,{"derivedFrom":makeQuery(id+"F21.opExtrude","SWEPT_EDGE",EDGE,{"disambiguationData":[OSD([sQuery(id+"F20.wireOp",EDGE,"E313"),sQuery(id+"F20.wireOp",EDGE,"E314")])]})});
            var Q4;
            Q4=makeQuery(id+"F21.boolean.opBoolean","COPY",EDGE,{"derivedFrom":makeQuery(id+"F21.opExtrude","SWEPT_EDGE",EDGE,{"disambiguationData":[OSD([sQuery(id+"F20.wireOp",EDGE,"E319"),sQuery(id+"F20.wireOp",EDGE,"E320")])]})});
            var Q5;
            Q5=makeQuery(id+"F21.boolean.opBoolean","COPY",EDGE,{"derivedFrom":makeQuery(id+"F21.opExtrude","SWEPT_EDGE",EDGE,{"disambiguationData":[OSD([sQuery(id+"F20.wireOp",EDGE,"E316"),sQuery(id+"F20.wireOp",EDGE,"E317")])]})});
            var Q6;
            Q6=makeQuery(id+"F21.boolean.opBoolean","COPY",EDGE,{"derivedFrom":makeQuery(id+"F21.opExtrude","SWEPT_EDGE",EDGE,{"disambiguationData":[OSD([sQuery(id+"F20.wireOp",EDGE,"E305"),sQuery(id+"F20.wireOp",EDGE,"E306")])]})});
            var Q7;
            Q7=makeQuery(id+"F21.boolean.opBoolean","COPY",EDGE,{"derivedFrom":makeQuery(id+"F21.opExtrude","SWEPT_EDGE",EDGE,{"disambiguationData":[OSD([sQuery(id+"F20.wireOp",EDGE,"E317"),sQuery(id+"F20.wireOp",EDGE,"E318")])]})});
            var Q8;
            Q8=makeQuery(id+"F21.boolean.opBoolean","COPY",EDGE,{"derivedFrom":makeQuery(id+"F21.opExtrude","SWEPT_EDGE",EDGE,{"disambiguationData":[OSD([sQuery(id+"F20.wireOp",EDGE,"E311"),sQuery(id+"F20.wireOp",EDGE,"E312")])]})});
            var Q9;
            Q9=makeQuery(id+"F21.boolean.opBoolean","COPY",EDGE,{"derivedFrom":makeQuery(id+"F21.opExtrude","SWEPT_EDGE",EDGE,{"disambiguationData":[OSD([sQuery(id+"F20.wireOp",EDGE,"E314"),sQuery(id+"F20.wireOp",EDGE,"E315")])]})});
            var Q10;
            Q10=makeQuery(id+"F21.boolean.opBoolean","COPY",EDGE,{"derivedFrom":makeQuery(id+"F21.opExtrude","SWEPT_EDGE",EDGE,{"disambiguationData":[OSD([sQuery(id+"F20.wireOp",EDGE,"E320"),sQuery(id+"F20.wireOp",EDGE,"E321")])]})});
            var Q11;
            Q11=makeQuery(id+"F21.boolean.opBoolean","COPY",EDGE,{"derivedFrom":makeQuery(id+"F21.opExtrude","SWEPT_EDGE",EDGE,{"disambiguationData":[OSD([sQuery(id+"F20.wireOp",EDGE,"E306"),sQuery(id+"F20.wireOp",EDGE,"E307")])]})});
            fillet(context, id + "F22", {"entities" : qUnion([Q0, Q1, Q2, Q3, Q4, Q5, Q6, Q7, Q8, Q9, Q10, Q11]), "radius" : 1 * mm, "allowEdgeOverflow" : false});
        }
        {
            var Q0;
            Q0=makeQuery(id+"F7.opExtrude","CAP_FACE",FACE,{"disambiguationData":[OSD([sQuery(id+"F5.wireOp",EDGE,"E101.0.0"),sQuery(id+"F5.wireOp",EDGE,"E101.0.1"),sQuery(id+"F5.wireOp",EDGE,"E101.0.2"),sQuery(id+"F5.wireOp",EDGE,"E101.0.3"),sQuery(id+"F5.wireOp",EDGE,"E101.0.4"),sQuery(id+"F5.wireOp",EDGE,"E101.0.8"),sQuery(id+"F5.wireOp",EDGE,"E101.0.9"),sQuery(id+"F5.wireOp",EDGE,"E101.0.10"),sQuery(id+"F5.wireOp",EDGE,"E101.0.11"),sQuery(id+"F5.wireOp",EDGE,"E101.0.12"),sQuery(id+"F5.wireOp",EDGE,"E101.0.13"),sQuery(id+"F5.wireOp",EDGE,"E101.0.14"),sQuery(id+"F5.wireOp",EDGE,"E101.0.18"),sQuery(id+"F5.wireOp",EDGE,"E101.0.19"),sQuery(id+"F5.wireOp",EDGE,"E102"),sQuery(id+"F5.wireOp",EDGE,"E103"),sQuery(id+"F5.wireOp",EDGE,"E104.0"),sQuery(id+"F5.wireOp",EDGE,"E105.0"),sQuery(id+"F5.wireOp",EDGE,"E106.0"),sQuery(id+"F5.wireOp",EDGE,"E107.0"),sQuery(id+"F5.wireOp",EDGE,"E108.0"),sQuery(id+"F5.wireOp",EDGE,"E109.0"),sQuery(id+"F5.wireOp",EDGE,"E110.0"),sQuery(id+"F5.wireOp",EDGE,"E111.0"),sQuery(id+"F5.wireOp",EDGE,"E112.0"),sQuery(id+"F5.wireOp",EDGE,"E113.0"),sQuery(id+"F5.wireOp",EDGE,"E114.0"),sQuery(id+"F5.wireOp",EDGE,"E115.0")])],"isStart":true});
            var Q1;
            Q1=makeQuery(id+"F6.opExtrude","CAP_FACE",FACE,{"disambiguationData":[OSD([sQuery(id+"F4.wireOp",EDGE,"E81.0"),sQuery(id+"F4.wireOp",EDGE,"E82.0"),sQuery(id+"F4.wireOp",EDGE,"E83.0"),sQuery(id+"F4.wireOp",EDGE,"E84.0"),sQuery(id+"F4.wireOp",EDGE,"E85.0"),sQuery(id+"F4.wireOp",EDGE,"E86.0"),sQuery(id+"F4.wireOp",EDGE,"E87.0"),sQuery(id+"F4.wireOp",EDGE,"E88.0"),sQuery(id+"F4.wireOp",EDGE,"E89.0"),sQuery(id+"F4.wireOp",EDGE,"E90.0"),sQuery(id+"F4.wireOp",EDGE,"E91.0"),sQuery(id+"F4.wireOp",EDGE,"E92.0"),sQuery(id+"F4.wireOp",EDGE,"E93.0"),sQuery(id+"F4.wireOp",EDGE,"E94.0"),sQuery(id+"F4.wireOp",EDGE,"E95"),sQuery(id+"F4.wireOp",EDGE,"E96"),sQuery(id+"F4.wireOp",EDGE,"E97"),sQuery(id+"F4.wireOp",EDGE,"E98"),sQuery(id+"F4.wireOp",EDGE,"E99"),sQuery(id+"F4.wireOp",EDGE,"E100")])],"isStart":true});
            var Q2;
            Q2=makeQuery(id+"F3.opExtrude","CAP_FACE",FACE,{"disambiguationData":[OSD([sQuery(id+"F2.wireOp",EDGE,"E36.0"),sQuery(id+"F2.wireOp",EDGE,"E37.0"),sQuery(id+"F2.wireOp",EDGE,"E38.0"),sQuery(id+"F2.wireOp",EDGE,"E39.0"),sQuery(id+"F2.wireOp",EDGE,"E40.0"),sQuery(id+"F2.wireOp",EDGE,"E41.0"),sQuery(id+"F2.wireOp",EDGE,"E42.0"),sQuery(id+"F2.wireOp",EDGE,"E43.0"),sQuery(id+"F2.wireOp",EDGE,"E44.0"),sQuery(id+"F2.wireOp",EDGE,"E45.0"),sQuery(id+"F2.wireOp",EDGE,"E46.0"),sQuery(id+"F2.wireOp",EDGE,"E47.bottom"),sQuery(id+"F2.wireOp",EDGE,"E47.top"),sQuery(id+"F2.wireOp",EDGE,"E47.left"),sQuery(id+"F2.wireOp",EDGE,"E47.right"),sQuery(id+"F2.wireOp",EDGE,"E48"),sQuery(id+"F2.wireOp",EDGE,"E49"),sQuery(id+"F2.wireOp",EDGE,"E50"),sQuery(id+"F2.wireOp",EDGE,"E51.MirrorCS"),sQuery(id+"F2.wireOp",EDGE,"E52.MirrorCS"),sQuery(id+"F2.wireOp",EDGE,"E53.MirrorCS"),sQuery(id+"F2.wireOp",EDGE,"E54"),sQuery(id+"F2.wireOp",EDGE,"E55.MirrorCS"),sQuery(id+"F2.wireOp",EDGE,"E57"),sQuery(id+"F2.wireOp",EDGE,"E63"),sQuery(id+"F2.wireOp",EDGE,"E65"),sQuery(id+"F2.wireOp",EDGE,"E67"),sQuery(id+"F2.wireOp",EDGE,"E69"),sQuery(id+"F2.wireOp",EDGE,"E72"),sQuery(id+"F2.wireOp",EDGE,"E75"),sQuery(id+"F2.wireOp",EDGE,"E78"),sQuery(id+"F2.wireOp",EDGE,"E79"),sQuery(id+"F2.wireOp",EDGE,"E80")])],"isStart":true});
            chamfer(context, id + "F23", {"entities" : qUnion([Q0, Q1, Q2]), "width" : 0.2 * mm});
        }
    });
